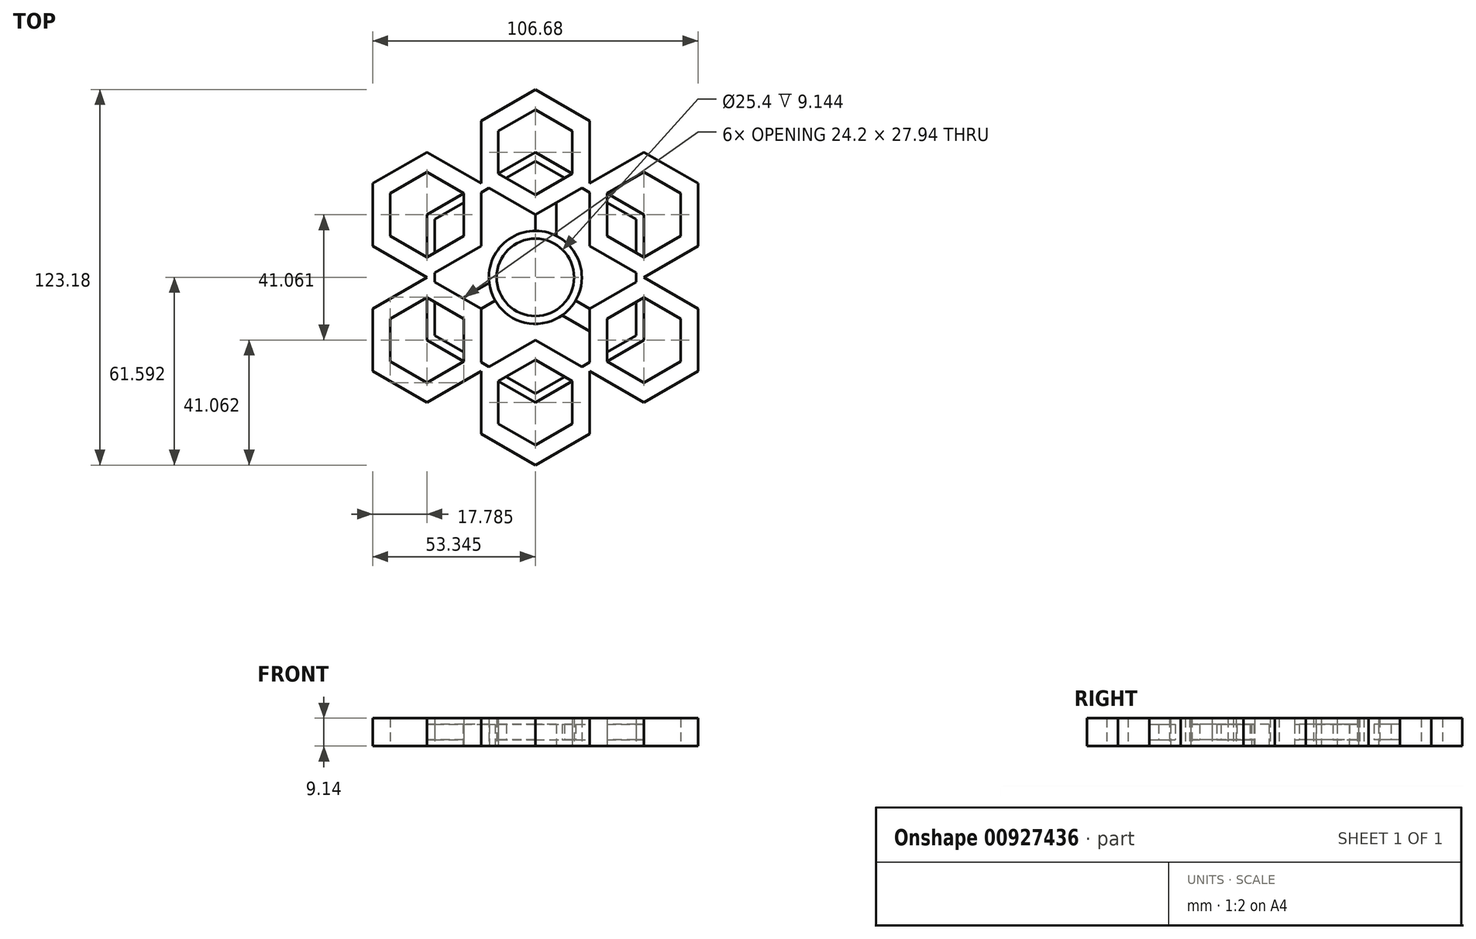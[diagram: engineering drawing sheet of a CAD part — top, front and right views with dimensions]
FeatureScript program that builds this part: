
annotation { "Feature Type Name" : "Feature", "Feature Type Description" : "" }
export const myFeature = defineFeature(function(context is Context, id is Id, definition is map)
    precondition{}
    {
        {
            var Q0;
            Q0=qCreatedBy(makeId("Top.planeOp"),FACE);
            var sketch = newSketch(context, id + "F0", { "sketchPlane" : qUnion([Q0])});
            skCircle(sketch, "E0", {"center": v(-0.28, 0.5) * mm, "radius": 12.7 * mm});
            skCircle(sketch, "E1.cCircle", {"center": v(-0.28, 0.5) * mm, "radius": 35.56 * mm, "construction": true});
            skLineSegment(sketch, "E1.0", {"start": v(35.28, 21.02) * mm, "end": v(35.28, -20.04) * mm});
            skLineSegment(sketch, "E1.1", {"start": v(35.28, -20.04) * mm, "end": v(-0.28, -40.57) * mm});
            skLineSegment(sketch, "E1.2", {"start": v(-0.28, -40.57) * mm, "end": v(-35.84, -20.04) * mm});
            skLineSegment(sketch, "E1.3", {"start": v(-35.84, -20.04) * mm, "end": v(-35.84, 21.02) * mm});
            skLineSegment(sketch, "E1.4", {"start": v(-35.84, 21.02) * mm, "end": v(-0.28, 41.55) * mm});
            skLineSegment(sketch, "E1.5", {"start": v(-0.28, 41.55) * mm, "end": v(35.28, 21.02) * mm});
            skPoint(sketch, "E1.0.midPoint", {"position": v(35.28, 0.5) * mm});
            skCircle(sketch, "E2.cCircle", {"center": v(35.28, 21.02) * mm, "radius": 20.53 * mm, "construction": true});
            skLineSegment(sketch, "E2.0", {"start": v(35.28, 0.5) * mm, "end": v(17.5, 10.76) * mm});
            skLineSegment(sketch, "E2.1", {"start": v(17.5, 10.76) * mm, "end": v(17.5, 31.29) * mm});
            skLineSegment(sketch, "E2.2", {"start": v(17.5, 31.29) * mm, "end": v(35.28, 41.55) * mm});
            skLineSegment(sketch, "E2.3", {"start": v(35.28, 41.55) * mm, "end": v(53.06, 31.29) * mm});
            skLineSegment(sketch, "E2.4", {"start": v(53.06, 31.29) * mm, "end": v(53.06, 10.76) * mm});
            skLineSegment(sketch, "E2.5", {"start": v(53.06, 10.76) * mm, "end": v(35.28, 0.5) * mm});
            skCircle(sketch, "E3.cCircle", {"center": v(-0.28, 41.55) * mm, "radius": 20.53 * mm, "construction": true});
            skLineSegment(sketch, "E3.0", {"start": v(17.5, 31.29) * mm, "end": v(-0.28, 21.02) * mm});
            skLineSegment(sketch, "E3.1", {"start": v(-0.28, 21.02) * mm, "end": v(-18.06, 31.29) * mm});
            skLineSegment(sketch, "E3.2", {"start": v(-18.06, 31.29) * mm, "end": v(-18.06, 51.82) * mm});
            skLineSegment(sketch, "E3.3", {"start": v(-18.06, 51.82) * mm, "end": v(-0.28, 62.08) * mm});
            skLineSegment(sketch, "E3.4", {"start": v(-0.28, 62.08) * mm, "end": v(17.5, 51.82) * mm});
            skLineSegment(sketch, "E3.5", {"start": v(17.5, 51.82) * mm, "end": v(17.5, 31.29) * mm});
            skCircle(sketch, "E4.cCircle", {"center": v(-35.84, 21.02) * mm, "radius": 20.53 * mm, "construction": true});
            skLineSegment(sketch, "E4.0", {"start": v(-18.06, 31.29) * mm, "end": v(-18.06, 10.76) * mm});
            skLineSegment(sketch, "E4.1", {"start": v(-18.06, 10.76) * mm, "end": v(-35.84, 0.5) * mm});
            skLineSegment(sketch, "E4.2", {"start": v(-35.84, 0.5) * mm, "end": v(-53.62, 10.76) * mm});
            skLineSegment(sketch, "E4.3", {"start": v(-53.62, 10.76) * mm, "end": v(-53.62, 31.29) * mm});
            skLineSegment(sketch, "E4.4", {"start": v(-53.62, 31.29) * mm, "end": v(-35.84, 41.55) * mm});
            skLineSegment(sketch, "E4.5", {"start": v(-35.84, 41.55) * mm, "end": v(-18.06, 31.29) * mm});
            skCircle(sketch, "E5.cCircle", {"center": v(-35.84, -20.04) * mm, "radius": 20.53 * mm, "construction": true});
            skLineSegment(sketch, "E5.0", {"start": v(-35.84, 0.5) * mm, "end": v(-18.06, -9.77) * mm});
            skLineSegment(sketch, "E5.1", {"start": v(-18.06, -9.77) * mm, "end": v(-18.06, -30.3) * mm});
            skLineSegment(sketch, "E5.2", {"start": v(-18.06, -30.3) * mm, "end": v(-35.84, -40.57) * mm});
            skLineSegment(sketch, "E5.3", {"start": v(-35.84, -40.57) * mm, "end": v(-53.62, -30.3) * mm});
            skLineSegment(sketch, "E5.4", {"start": v(-53.62, -30.3) * mm, "end": v(-53.62, -9.77) * mm});
            skLineSegment(sketch, "E5.5", {"start": v(-53.62, -9.77) * mm, "end": v(-35.84, 0.5) * mm});
            skCircle(sketch, "E6.cCircle", {"center": v(-0.28, -40.57) * mm, "radius": 20.53 * mm, "construction": true});
            skLineSegment(sketch, "E6.0", {"start": v(-18.06, -30.3) * mm, "end": v(-0.28, -20.04) * mm});
            skLineSegment(sketch, "E6.1", {"start": v(-0.28, -20.04) * mm, "end": v(17.5, -30.3) * mm});
            skLineSegment(sketch, "E6.2", {"start": v(17.5, -30.3) * mm, "end": v(17.5, -50.83) * mm});
            skLineSegment(sketch, "E6.3", {"start": v(17.5, -50.83) * mm, "end": v(-0.28, -61.1) * mm});
            skLineSegment(sketch, "E6.4", {"start": v(-0.28, -61.1) * mm, "end": v(-18.06, -50.83) * mm});
            skLineSegment(sketch, "E6.5", {"start": v(-18.06, -50.83) * mm, "end": v(-18.06, -30.3) * mm});
            skCircle(sketch, "E7.cCircle", {"center": v(35.28, -20.04) * mm, "radius": 20.53 * mm, "construction": true});
            skLineSegment(sketch, "E7.0", {"start": v(35.28, 0.5) * mm, "end": v(53.06, -9.77) * mm});
            skLineSegment(sketch, "E7.1", {"start": v(53.06, -9.77) * mm, "end": v(53.06, -30.3) * mm});
            skLineSegment(sketch, "E7.2", {"start": v(53.06, -30.3) * mm, "end": v(35.28, -40.57) * mm});
            skLineSegment(sketch, "E7.3", {"start": v(35.28, -40.57) * mm, "end": v(17.5, -30.3) * mm});
            skLineSegment(sketch, "E7.4", {"start": v(17.5, -30.3) * mm, "end": v(17.5, -9.77) * mm});
            skLineSegment(sketch, "E7.5", {"start": v(17.5, -9.77) * mm, "end": v(35.28, 0.5) * mm});
            skCircle(sketch, "E8.cCircle", {"center": v(-35.84, 21.02) * mm, "radius": 13.97 * mm, "construction": true});
            skLineSegment(sketch, "E8.0", {"start": v(-35.84, 7.05) * mm, "end": v(-47.93, 14.04) * mm});
            skLineSegment(sketch, "E8.1", {"start": v(-47.93, 14.04) * mm, "end": v(-47.93, 28) * mm});
            skLineSegment(sketch, "E8.2", {"start": v(-47.93, 28) * mm, "end": v(-35.84, 35) * mm});
            skLineSegment(sketch, "E8.3", {"start": v(-35.84, 35) * mm, "end": v(-23.74, 28) * mm});
            skLineSegment(sketch, "E8.4", {"start": v(-23.74, 28) * mm, "end": v(-23.74, 14.04) * mm});
            skLineSegment(sketch, "E8.5", {"start": v(-23.74, 14.04) * mm, "end": v(-35.84, 7.05) * mm});
            skCircle(sketch, "E9.cCircle", {"center": v(-0.28, 41.55) * mm, "radius": 13.97 * mm, "construction": true});
            skLineSegment(sketch, "E9.0", {"start": v(-0.28, 55.52) * mm, "end": v(11.82, 48.54) * mm});
            skLineSegment(sketch, "E9.1", {"start": v(11.82, 48.54) * mm, "end": v(11.82, 34.57) * mm});
            skLineSegment(sketch, "E9.2", {"start": v(11.82, 34.57) * mm, "end": v(-0.28, 27.58) * mm});
            skLineSegment(sketch, "E9.3", {"start": v(-0.28, 27.58) * mm, "end": v(-12.37, 34.57) * mm});
            skLineSegment(sketch, "E9.4", {"start": v(-12.37, 34.57) * mm, "end": v(-12.37, 48.54) * mm});
            skLineSegment(sketch, "E9.5", {"start": v(-12.37, 48.54) * mm, "end": v(-0.28, 55.52) * mm});
            skCircle(sketch, "E10.cCircle", {"center": v(35.28, 21.02) * mm, "radius": 13.97 * mm, "construction": true});
            skLineSegment(sketch, "E10.0", {"start": v(35.28, 7.05) * mm, "end": v(23.19, 14.04) * mm});
            skLineSegment(sketch, "E10.1", {"start": v(23.19, 14.04) * mm, "end": v(23.19, 28) * mm});
            skLineSegment(sketch, "E10.2", {"start": v(23.19, 28) * mm, "end": v(35.28, 35) * mm});
            skLineSegment(sketch, "E10.3", {"start": v(35.28, 35) * mm, "end": v(47.38, 28) * mm});
            skLineSegment(sketch, "E10.4", {"start": v(47.38, 28) * mm, "end": v(47.38, 14.04) * mm});
            skLineSegment(sketch, "E10.5", {"start": v(47.38, 14.04) * mm, "end": v(35.28, 7.05) * mm});
            skCircle(sketch, "E11.cCircle", {"center": v(35.28, -20.04) * mm, "radius": 13.97 * mm, "construction": true});
            skLineSegment(sketch, "E11.0", {"start": v(35.28, -34) * mm, "end": v(23.19, -27.02) * mm});
            skLineSegment(sketch, "E11.1", {"start": v(23.19, -27.02) * mm, "end": v(23.19, -13.05) * mm});
            skLineSegment(sketch, "E11.2", {"start": v(23.19, -13.05) * mm, "end": v(35.28, -6.07) * mm});
            skLineSegment(sketch, "E11.3", {"start": v(35.28, -6.07) * mm, "end": v(47.38, -13.05) * mm});
            skLineSegment(sketch, "E11.4", {"start": v(47.38, -13.05) * mm, "end": v(47.38, -27.02) * mm});
            skLineSegment(sketch, "E11.5", {"start": v(47.38, -27.02) * mm, "end": v(35.28, -34) * mm});
            skCircle(sketch, "E12.cCircle", {"center": v(-0.28, -40.57) * mm, "radius": 12.1 * mm, "construction": true});
            skLineSegment(sketch, "E12.0", {"start": v(-0.28, -54.54) * mm, "end": v(-12.37, -47.55) * mm});
            skLineSegment(sketch, "E12.1", {"start": v(-12.37, -47.55) * mm, "end": v(-12.37, -33.58) * mm});
            skLineSegment(sketch, "E12.2", {"start": v(-12.37, -33.58) * mm, "end": v(-0.28, -26.6) * mm});
            skLineSegment(sketch, "E12.3", {"start": v(-0.28, -26.6) * mm, "end": v(11.82, -33.58) * mm});
            skLineSegment(sketch, "E12.4", {"start": v(11.82, -33.58) * mm, "end": v(11.82, -47.55) * mm});
            skLineSegment(sketch, "E12.5", {"start": v(11.82, -47.55) * mm, "end": v(-0.28, -54.54) * mm});
            skPoint(sketch, "E12.0.midPoint", {"position": v(-6.32, -51.05) * mm});
            skCircle(sketch, "E13.cCircle", {"center": v(-35.84, -20.04) * mm, "radius": 13.97 * mm, "construction": true});
            skLineSegment(sketch, "E13.0", {"start": v(-35.84, -6.07) * mm, "end": v(-23.74, -13.05) * mm});
            skLineSegment(sketch, "E13.1", {"start": v(-23.74, -13.05) * mm, "end": v(-23.74, -27.02) * mm});
            skLineSegment(sketch, "E13.2", {"start": v(-23.74, -27.02) * mm, "end": v(-35.84, -34) * mm});
            skLineSegment(sketch, "E13.3", {"start": v(-35.84, -34) * mm, "end": v(-47.93, -27.02) * mm});
            skLineSegment(sketch, "E13.4", {"start": v(-47.93, -27.02) * mm, "end": v(-47.93, -13.05) * mm});
            skLineSegment(sketch, "E13.5", {"start": v(-47.93, -13.05) * mm, "end": v(-35.84, -6.07) * mm});
            skLineSegment(sketch, "E14", {"start": v(-18.06, -9.77) * mm, "end": v(-0.28, 0.5) * mm});
            skLineSegment(sketch, "E15", {"start": v(-0.28, 21.02) * mm, "end": v(-0.28, 0.5) * mm});
            skLineSegment(sketch, "E16", {"start": v(-0.28, 0.5) * mm, "end": v(17.5, -9.77) * mm});
            skLineSegment(sketch, "E17", {"start": v(-0.28, 0.5) * mm, "end": v(-0.28, -6.88) * mm});
            skLineSegment(sketch, "E18", {"start": v(-0.28, -6.88) * mm, "end": v(-0.28, 0.5) * mm});
            skLineSegment(sketch, "E19", {"start": v(-0.28, 0.5) * mm, "end": v(6.6, 4.46) * mm});
            skLineSegment(sketch, "E20", {"start": v(-0.28, 0.5) * mm, "end": v(-6.27, 3.95) * mm});
            skLineSegment(sketch, "E21", {"start": v(-6.27, 3.95) * mm, "end": v(-24.05, -6.31) * mm});
            skLineSegment(sketch, "E22", {"start": v(6.6, 4.46) * mm, "end": v(6.6, 24.99) * mm});
            skLineSegment(sketch, "E23", {"start": v(-0.28, -6.88) * mm, "end": v(17.5, -17.14) * mm});
            skCircle(sketch, "E24", {"center": v(-0.28, 0.5) * mm, "radius": 15.24 * mm});
            skCircle(sketch, "E25.cCircle", {"center": v(-0.28, 0.5) * mm, "radius": 38.1 * mm, "construction": true});
            skLineSegment(sketch, "E25.0", {"start": v(-0.28, 38.6) * mm, "end": v(32.72, 19.54) * mm});
            skLineSegment(sketch, "E25.1", {"start": v(32.72, 19.54) * mm, "end": v(32.72, -18.56) * mm});
            skLineSegment(sketch, "E25.2", {"start": v(32.72, -18.56) * mm, "end": v(-0.28, -37.6) * mm});
            skLineSegment(sketch, "E25.3", {"start": v(-0.28, -37.6) * mm, "end": v(-33.27, -18.56) * mm});
            skLineSegment(sketch, "E25.4", {"start": v(-33.27, -18.56) * mm, "end": v(-33.27, 19.54) * mm});
            skLineSegment(sketch, "E25.5", {"start": v(-33.27, 19.54) * mm, "end": v(-0.28, 38.6) * mm});
            skSolve(sketch);
        }
        {
            var Q0;
            {var subQ0=sQuery(id+"F0.wireOp",EDGE,"E4.2");Q0=makeQuery(id+"F0.imprint","IMPRINT",FACE,{"disambiguationData":[TD([[makeQuery(id+"F0.imprint","IMPRINT",EDGE,{"derivedFrom":subQ0}),-1.0]])]});}
            var Q1;
            {var subQ0=sQuery(id+"F0.wireOp",EDGE,"E4.1");var subQ5=sQuery(id+"F0.wireOp",EDGE,"E25.4");var subQ6=makeQuery(id+"F0.imprint","INTERSECT",VERTEX,{"derivedFrom":[subQ0,subQ5]});Q1=makeQuery(id+"F0.imprint","IMPRINT",FACE,{"disambiguationData":[TD([[makeQuery(id+"F0.imprint","IMPRINT",EDGE,{"disambiguationData":[TD([[subQ6,-1.0]])],"derivedFrom":subQ5}),1.0]])]});}
            var Q2;
            {var subQ3=sQuery(id+"F0.wireOp",EDGE,"E25.4");var subQ9=sQuery(id+"F0.wireOp",EDGE,"E25.5");var subQ11=makeQuery(id+"F0.imprint","INTERSECT",VERTEX,{"derivedFrom":[subQ3,subQ9]});Q2=makeQuery(id+"F0.imprint","IMPRINT",FACE,{"disambiguationData":[TD([[makeQuery(id+"F0.imprint","IMPRINT",EDGE,{"disambiguationData":[TD([[subQ11,1.0]])],"derivedFrom":subQ3}),1.0]])]});}
            var Q3;
            {var subQ0=sQuery(id+"F0.wireOp",EDGE,"E4.0");var subQ5=sQuery(id+"F0.wireOp",EDGE,"E25.5");var subQ6=makeQuery(id+"F0.imprint","INTERSECT",VERTEX,{"derivedFrom":[subQ0,subQ5]});Q3=makeQuery(id+"F0.imprint","IMPRINT",FACE,{"disambiguationData":[TD([[makeQuery(id+"F0.imprint","IMPRINT",EDGE,{"disambiguationData":[TD([[subQ6,1.0]])],"derivedFrom":subQ5}),1.0]])]});}
            var Q4;
            {var subQ7=sQuery(id+"F0.wireOp",EDGE,"E4.1");var subQ8=sQuery(id+"F0.wireOp",EDGE,"E4.0");var subQ9=makeQuery(id+"F0.imprint","INTERSECT",VERTEX,{"derivedFrom":[subQ8,subQ7]});Q4=makeQuery(id+"F0.imprint","IMPRINT",FACE,{"disambiguationData":[TD([[makeQuery(id+"F0.imprint","IMPRINT",EDGE,{"disambiguationData":[TD([[subQ9,1.0]])],"derivedFrom":subQ8}),-1.0]])]});}
            var Q5;
            {var subQ1=sQuery(id+"F0.wireOp",EDGE,"E4.1");var subQ3=sQuery(id+"F0.wireOp",EDGE,"E25.4");var subQ4=makeQuery(id+"F0.imprint","INTERSECT",VERTEX,{"derivedFrom":[subQ1,subQ3]});Q5=makeQuery(id+"F0.imprint","IMPRINT",FACE,{"disambiguationData":[TD([[makeQuery(id+"F0.imprint","IMPRINT",EDGE,{"disambiguationData":[TD([[subQ4,1.0]])],"derivedFrom":subQ3}),1.0]])]});}
            var Q6;
            {var subQ0=sQuery(id+"F0.wireOp",EDGE,"E5.0");var subQ5=sQuery(id+"F0.wireOp",EDGE,"E25.4");var subQ6=makeQuery(id+"F0.imprint","INTERSECT",VERTEX,{"derivedFrom":[subQ0,subQ5]});Q6=makeQuery(id+"F0.imprint","IMPRINT",FACE,{"disambiguationData":[TD([[makeQuery(id+"F0.imprint","IMPRINT",EDGE,{"disambiguationData":[TD([[subQ6,1.0]])],"derivedFrom":subQ5}),1.0]])]});}
            var Q7;
            {var subQ0=sQuery(id+"F0.wireOp",EDGE,"E5.2");Q7=makeQuery(id+"F0.imprint","IMPRINT",FACE,{"disambiguationData":[TD([[makeQuery(id+"F0.imprint","IMPRINT",EDGE,{"derivedFrom":subQ0}),-1.0]])]});}
            var Q8;
            {var subQ1=sQuery(id+"F0.wireOp",EDGE,"E5.0");var subQ10=makeQuery(id+"F0.imprint","INTERSECT",VERTEX,{"derivedFrom":[subQ1,sQuery(id+"F0.wireOp",EDGE,"E21")]});Q8=makeQuery(id+"F0.imprint","IMPRINT",FACE,{"disambiguationData":[TD([[makeQuery(id+"F0.imprint","IMPRINT",EDGE,{"disambiguationData":[TD([[subQ10,1.0]])],"derivedFrom":subQ1}),-1.0]])]});}
            var Q9;
            {var subQ3=sQuery(id+"F0.wireOp",EDGE,"E25.3");var subQ8=sQuery(id+"F0.wireOp",EDGE,"E25.4");var subQ10=makeQuery(id+"F0.imprint","INTERSECT",VERTEX,{"derivedFrom":[subQ3,subQ8]});Q9=makeQuery(id+"F0.imprint","IMPRINT",FACE,{"disambiguationData":[TD([[makeQuery(id+"F0.imprint","IMPRINT",EDGE,{"disambiguationData":[TD([[subQ10,1.0]])],"derivedFrom":subQ3}),1.0]])]});}
            var Q10;
            {var subQ0=sQuery(id+"F0.wireOp",EDGE,"E5.1");var subQ5=sQuery(id+"F0.wireOp",EDGE,"E25.3");var subQ6=makeQuery(id+"F0.imprint","INTERSECT",VERTEX,{"derivedFrom":[subQ0,subQ5]});Q10=makeQuery(id+"F0.imprint","IMPRINT",FACE,{"disambiguationData":[TD([[makeQuery(id+"F0.imprint","IMPRINT",EDGE,{"disambiguationData":[TD([[subQ6,-1.0]])],"derivedFrom":subQ5}),1.0]])]});}
            var Q11;
            {var subQ1=sQuery(id+"F0.wireOp",EDGE,"E5.0");var subQ3=sQuery(id+"F0.wireOp",EDGE,"E21");var subQ4=makeQuery(id+"F0.imprint","INTERSECT",VERTEX,{"derivedFrom":[subQ1,subQ3]});Q11=makeQuery(id+"F0.imprint","IMPRINT",FACE,{"disambiguationData":[TD([[makeQuery(id+"F0.imprint","IMPRINT",EDGE,{"disambiguationData":[TD([[subQ4,1.0]])],"derivedFrom":subQ3}),1.0]])]});}
            var Q12;
            {var subQ0=sQuery(id+"F0.wireOp",EDGE,"E21");var subQ1=sQuery(id+"F0.wireOp",EDGE,"E0");var subQ2=makeQuery(id+"F0.imprint","INTERSECT",VERTEX,{"derivedFrom":[subQ1,subQ0]});Q12=makeQuery(id+"F0.imprint","IMPRINT",FACE,{"disambiguationData":[TD([[makeQuery(id+"F0.imprint","IMPRINT",EDGE,{"disambiguationData":[TD([[subQ2,-1.0]])],"derivedFrom":subQ1}),-1.0]])]});}
            var Q13;
            {var subQ0=sQuery(id+"F0.wireOp",EDGE,"E15");var subQ1=sQuery(id+"F0.wireOp",EDGE,"E0");var subQ2=makeQuery(id+"F0.imprint","INTERSECT",VERTEX,{"derivedFrom":[subQ1,subQ0]});Q13=makeQuery(id+"F0.imprint","IMPRINT",FACE,{"disambiguationData":[TD([[makeQuery(id+"F0.imprint","IMPRINT",EDGE,{"disambiguationData":[TD([[subQ2,-1.0]])],"derivedFrom":subQ1}),-1.0]])]});}
            var Q14;
            {var subQ0=sQuery(id+"F0.wireOp",EDGE,"E15");var subQ1=sQuery(id+"F0.wireOp",EDGE,"E0");var subQ2=makeQuery(id+"F0.imprint","INTERSECT",VERTEX,{"derivedFrom":[subQ1,subQ0]});Q14=makeQuery(id+"F0.imprint","IMPRINT",FACE,{"disambiguationData":[TD([[makeQuery(id+"F0.imprint","IMPRINT",EDGE,{"disambiguationData":[TD([[subQ2,1.0]])],"derivedFrom":subQ1}),-1.0]])]});}
            var Q15;
            {var subQ1=sQuery(id+"F0.wireOp",EDGE,"E3.0");var subQ3=sQuery(id+"F0.wireOp",EDGE,"E22");var subQ4=makeQuery(id+"F0.imprint","INTERSECT",VERTEX,{"derivedFrom":[subQ1,subQ3]});Q15=makeQuery(id+"F0.imprint","IMPRINT",FACE,{"disambiguationData":[TD([[makeQuery(id+"F0.imprint","IMPRINT",EDGE,{"disambiguationData":[TD([[subQ4,1.0]])],"derivedFrom":subQ3}),1.0]])]});}
            var Q16;
            {var subQ0=sQuery(id+"F0.wireOp",EDGE,"E22");var subQ1=sQuery(id+"F0.wireOp",EDGE,"E0");var subQ2=makeQuery(id+"F0.imprint","INTERSECT",VERTEX,{"derivedFrom":[subQ1,subQ0]});Q16=makeQuery(id+"F0.imprint","IMPRINT",FACE,{"disambiguationData":[TD([[makeQuery(id+"F0.imprint","IMPRINT",EDGE,{"disambiguationData":[TD([[subQ2,1.0]])],"derivedFrom":subQ1}),-1.0]])]});}
            var Q17;
            {var subQ0=sQuery(id+"F0.wireOp",EDGE,"E23");var subQ1=sQuery(id+"F0.wireOp",EDGE,"E0");var subQ2=makeQuery(id+"F0.imprint","INTERSECT",VERTEX,{"derivedFrom":[subQ1,subQ0]});Q17=makeQuery(id+"F0.imprint","IMPRINT",FACE,{"disambiguationData":[TD([[makeQuery(id+"F0.imprint","IMPRINT",EDGE,{"disambiguationData":[TD([[subQ2,-1.0]])],"derivedFrom":subQ1}),-1.0]])]});}
            var Q18;
            {var subQ0=sQuery(id+"F0.wireOp",EDGE,"E14");var subQ1=sQuery(id+"F0.wireOp",EDGE,"E0");var subQ2=makeQuery(id+"F0.imprint","INTERSECT",VERTEX,{"derivedFrom":[subQ1,subQ0]});Q18=makeQuery(id+"F0.imprint","IMPRINT",FACE,{"disambiguationData":[TD([[makeQuery(id+"F0.imprint","IMPRINT",EDGE,{"disambiguationData":[TD([[subQ2,-1.0]])],"derivedFrom":subQ1}),-1.0]])]});}
            var Q19;
            {var subQ1=sQuery(id+"F0.wireOp",EDGE,"E7.4");var subQ3=sQuery(id+"F0.wireOp",EDGE,"E23");var subQ4=makeQuery(id+"F0.imprint","INTERSECT",VERTEX,{"derivedFrom":[subQ1,subQ3]});Q19=makeQuery(id+"F0.imprint","IMPRINT",FACE,{"disambiguationData":[TD([[makeQuery(id+"F0.imprint","IMPRINT",EDGE,{"disambiguationData":[TD([[subQ4,1.0]])],"derivedFrom":subQ3}),1.0]])]});}
            var Q20;
            {var subQ1=sQuery(id+"F0.wireOp",EDGE,"E5.1");var subQ3=sQuery(id+"F0.wireOp",EDGE,"E25.3");var subQ4=makeQuery(id+"F0.imprint","INTERSECT",VERTEX,{"derivedFrom":[subQ1,subQ3]});Q20=makeQuery(id+"F0.imprint","IMPRINT",FACE,{"disambiguationData":[TD([[makeQuery(id+"F0.imprint","IMPRINT",EDGE,{"disambiguationData":[TD([[subQ4,1.0]])],"derivedFrom":subQ3}),1.0]])]});}
            var Q21;
            {var subQ0=sQuery(id+"F0.wireOp",EDGE,"E6.0");var subQ5=sQuery(id+"F0.wireOp",EDGE,"E25.3");var subQ7=makeQuery(id+"F0.imprint","INTERSECT",VERTEX,{"derivedFrom":[subQ0,subQ5]});Q21=makeQuery(id+"F0.imprint","IMPRINT",FACE,{"disambiguationData":[TD([[makeQuery(id+"F0.imprint","IMPRINT",EDGE,{"disambiguationData":[TD([[subQ7,1.0]])],"derivedFrom":subQ5}),1.0]])]});}
            var Q22;
            {var subQ6=sQuery(id+"F0.wireOp",EDGE,"E6.0");var subQ9=sQuery(id+"F0.wireOp",EDGE,"E6.1");var subQ10=makeQuery(id+"F0.imprint","INTERSECT",VERTEX,{"derivedFrom":[subQ6,subQ9]});Q22=makeQuery(id+"F0.imprint","IMPRINT",FACE,{"disambiguationData":[TD([[makeQuery(id+"F0.imprint","IMPRINT",EDGE,{"disambiguationData":[TD([[subQ10,1.0]])],"derivedFrom":subQ6}),-1.0]])]});}
            var Q23;
            {var subQ0=sQuery(id+"F0.wireOp",EDGE,"E6.2");Q23=makeQuery(id+"F0.imprint","IMPRINT",FACE,{"disambiguationData":[TD([[makeQuery(id+"F0.imprint","IMPRINT",EDGE,{"derivedFrom":subQ0}),-1.0]])]});}
            var Q24;
            {var subQ3=sQuery(id+"F0.wireOp",EDGE,"E25.3");var subQ5=sQuery(id+"F0.wireOp",EDGE,"E25.2");var subQ6=makeQuery(id+"F0.imprint","INTERSECT",VERTEX,{"derivedFrom":[subQ5,subQ3]});Q24=makeQuery(id+"F0.imprint","IMPRINT",FACE,{"disambiguationData":[TD([[makeQuery(id+"F0.imprint","IMPRINT",EDGE,{"disambiguationData":[TD([[subQ6,1.0]])],"derivedFrom":subQ5}),1.0]])]});}
            var Q25;
            {var subQ0=sQuery(id+"F0.wireOp",EDGE,"E6.1");var subQ5=sQuery(id+"F0.wireOp",EDGE,"E25.2");var subQ6=makeQuery(id+"F0.imprint","INTERSECT",VERTEX,{"derivedFrom":[subQ0,subQ5]});Q25=makeQuery(id+"F0.imprint","IMPRINT",FACE,{"disambiguationData":[TD([[makeQuery(id+"F0.imprint","IMPRINT",EDGE,{"disambiguationData":[TD([[subQ6,-1.0]])],"derivedFrom":subQ5}),1.0]])]});}
            var Q26;
            {var subQ1=sQuery(id+"F0.wireOp",EDGE,"E7.4");var subQ9=makeQuery(id+"F0.imprint","INTERSECT",VERTEX,{"derivedFrom":[subQ1,sQuery(id+"F0.wireOp",EDGE,"E23")]});Q26=makeQuery(id+"F0.imprint","IMPRINT",FACE,{"disambiguationData":[TD([[makeQuery(id+"F0.imprint","IMPRINT",EDGE,{"disambiguationData":[TD([[subQ9,1.0]])],"derivedFrom":subQ1}),-1.0]])]});}
            var Q27;
            {var subQ0=sQuery(id+"F0.wireOp",EDGE,"E7.4");var subQ5=sQuery(id+"F0.wireOp",EDGE,"E25.2");var subQ6=makeQuery(id+"F0.imprint","INTERSECT",VERTEX,{"derivedFrom":[subQ0,subQ5]});Q27=makeQuery(id+"F0.imprint","IMPRINT",FACE,{"disambiguationData":[TD([[makeQuery(id+"F0.imprint","IMPRINT",EDGE,{"disambiguationData":[TD([[subQ6,1.0]])],"derivedFrom":subQ5}),1.0]])]});}
            var Q28;
            {var subQ1=sQuery(id+"F0.wireOp",EDGE,"E6.1");var subQ3=sQuery(id+"F0.wireOp",EDGE,"E25.2");var subQ4=makeQuery(id+"F0.imprint","INTERSECT",VERTEX,{"derivedFrom":[subQ1,subQ3]});Q28=makeQuery(id+"F0.imprint","IMPRINT",FACE,{"disambiguationData":[TD([[makeQuery(id+"F0.imprint","IMPRINT",EDGE,{"disambiguationData":[TD([[subQ4,1.0]])],"derivedFrom":subQ3}),1.0]])]});}
            var Q29;
            {var subQ0=sQuery(id+"F0.wireOp",EDGE,"E7.5");var subQ5=sQuery(id+"F0.wireOp",EDGE,"E25.1");var subQ6=makeQuery(id+"F0.imprint","INTERSECT",VERTEX,{"derivedFrom":[subQ0,subQ5]});Q29=makeQuery(id+"F0.imprint","IMPRINT",FACE,{"disambiguationData":[TD([[makeQuery(id+"F0.imprint","IMPRINT",EDGE,{"disambiguationData":[TD([[subQ6,-1.0]])],"derivedFrom":subQ5}),1.0]])]});}
            var Q30;
            {var subQ0=sQuery(id+"F0.wireOp",EDGE,"E7.0");Q30=makeQuery(id+"F0.imprint","IMPRINT",FACE,{"disambiguationData":[TD([[makeQuery(id+"F0.imprint","IMPRINT",EDGE,{"derivedFrom":subQ0}),-1.0]])]});}
            var Q31;
            {var subQ3=sQuery(id+"F0.wireOp",EDGE,"E25.2");var subQ9=sQuery(id+"F0.wireOp",EDGE,"E25.1");var subQ11=makeQuery(id+"F0.imprint","INTERSECT",VERTEX,{"derivedFrom":[subQ9,subQ3]});Q31=makeQuery(id+"F0.imprint","IMPRINT",FACE,{"disambiguationData":[TD([[makeQuery(id+"F0.imprint","IMPRINT",EDGE,{"disambiguationData":[TD([[subQ11,1.0]])],"derivedFrom":subQ9}),1.0]])]});}
            var Q32;
            {var subQ1=sQuery(id+"F0.wireOp",EDGE,"E2.0");var subQ3=sQuery(id+"F0.wireOp",EDGE,"E25.1");var subQ4=makeQuery(id+"F0.imprint","INTERSECT",VERTEX,{"derivedFrom":[subQ1,subQ3]});Q32=makeQuery(id+"F0.imprint","IMPRINT",FACE,{"disambiguationData":[TD([[makeQuery(id+"F0.imprint","IMPRINT",EDGE,{"disambiguationData":[TD([[subQ4,-1.0]])],"derivedFrom":subQ3}),1.0]])]});}
            var Q33;
            {var subQ0=sQuery(id+"F0.wireOp",EDGE,"E2.0");var subQ5=sQuery(id+"F0.wireOp",EDGE,"E25.1");var subQ7=makeQuery(id+"F0.imprint","INTERSECT",VERTEX,{"derivedFrom":[subQ0,subQ5]});Q33=makeQuery(id+"F0.imprint","IMPRINT",FACE,{"disambiguationData":[TD([[makeQuery(id+"F0.imprint","IMPRINT",EDGE,{"disambiguationData":[TD([[subQ7,1.0]])],"derivedFrom":subQ5}),1.0]])]});}
            var Q34;
            {var subQ7=sQuery(id+"F0.wireOp",EDGE,"E2.1");var subQ8=sQuery(id+"F0.wireOp",EDGE,"E2.0");var subQ9=makeQuery(id+"F0.imprint","INTERSECT",VERTEX,{"derivedFrom":[subQ8,subQ7]});Q34=makeQuery(id+"F0.imprint","IMPRINT",FACE,{"disambiguationData":[TD([[makeQuery(id+"F0.imprint","IMPRINT",EDGE,{"disambiguationData":[TD([[subQ9,1.0]])],"derivedFrom":subQ8}),-1.0]])]});}
            var Q35;
            {var subQ1=sQuery(id+"F0.wireOp",EDGE,"E2.2");Q35=makeQuery(id+"F0.imprint","IMPRINT",FACE,{"disambiguationData":[TD([[makeQuery(id+"F0.imprint","IMPRINT",EDGE,{"derivedFrom":subQ1}),-1.0]])]});}
            var Q36;
            {var subQ3=sQuery(id+"F0.wireOp",EDGE,"E25.0");var subQ8=sQuery(id+"F0.wireOp",EDGE,"E25.1");var subQ11=makeQuery(id+"F0.imprint","INTERSECT",VERTEX,{"derivedFrom":[subQ3,subQ8]});Q36=makeQuery(id+"F0.imprint","IMPRINT",FACE,{"disambiguationData":[TD([[makeQuery(id+"F0.imprint","IMPRINT",EDGE,{"disambiguationData":[TD([[subQ11,1.0]])],"derivedFrom":subQ3}),1.0]])]});}
            var Q37;
            {var subQ0=sQuery(id+"F0.wireOp",EDGE,"E2.1");var subQ5=sQuery(id+"F0.wireOp",EDGE,"E25.0");var subQ6=makeQuery(id+"F0.imprint","INTERSECT",VERTEX,{"derivedFrom":[subQ0,subQ5]});Q37=makeQuery(id+"F0.imprint","IMPRINT",FACE,{"disambiguationData":[TD([[makeQuery(id+"F0.imprint","IMPRINT",EDGE,{"disambiguationData":[TD([[subQ6,-1.0]])],"derivedFrom":subQ5}),1.0]])]});}
            var Q38;
            {var subQ1=sQuery(id+"F0.wireOp",EDGE,"E2.1");var subQ3=sQuery(id+"F0.wireOp",EDGE,"E25.0");var subQ4=makeQuery(id+"F0.imprint","INTERSECT",VERTEX,{"derivedFrom":[subQ1,subQ3]});Q38=makeQuery(id+"F0.imprint","IMPRINT",FACE,{"disambiguationData":[TD([[makeQuery(id+"F0.imprint","IMPRINT",EDGE,{"disambiguationData":[TD([[subQ4,1.0]])],"derivedFrom":subQ3}),1.0]])]});}
            var Q39;
            {var subQ0=sQuery(id+"F0.wireOp",EDGE,"E3.0");var subQ5=sQuery(id+"F0.wireOp",EDGE,"E25.0");var subQ6=makeQuery(id+"F0.imprint","INTERSECT",VERTEX,{"derivedFrom":[subQ0,subQ5]});Q39=makeQuery(id+"F0.imprint","IMPRINT",FACE,{"disambiguationData":[TD([[makeQuery(id+"F0.imprint","IMPRINT",EDGE,{"disambiguationData":[TD([[subQ6,1.0]])],"derivedFrom":subQ5}),1.0]])]});}
            var Q40;
            {var subQ6=sQuery(id+"F0.wireOp",EDGE,"E3.0");var subQ11=makeQuery(id+"F0.imprint","INTERSECT",VERTEX,{"derivedFrom":[subQ6,sQuery(id+"F0.wireOp",EDGE,"E22")]});Q40=makeQuery(id+"F0.imprint","IMPRINT",FACE,{"disambiguationData":[TD([[makeQuery(id+"F0.imprint","IMPRINT",EDGE,{"disambiguationData":[TD([[subQ11,1.0]])],"derivedFrom":subQ6}),-1.0]])]});}
            var Q41;
            {var subQ0=sQuery(id+"F0.wireOp",EDGE,"E3.2");Q41=makeQuery(id+"F0.imprint","IMPRINT",FACE,{"disambiguationData":[TD([[makeQuery(id+"F0.imprint","IMPRINT",EDGE,{"derivedFrom":subQ0}),-1.0]])]});}
            var Q42;
            {var subQ3=sQuery(id+"F0.wireOp",EDGE,"E25.5");var subQ8=sQuery(id+"F0.wireOp",EDGE,"E25.0");var subQ11=makeQuery(id+"F0.imprint","INTERSECT",VERTEX,{"derivedFrom":[subQ8,subQ3]});Q42=makeQuery(id+"F0.imprint","IMPRINT",FACE,{"disambiguationData":[TD([[makeQuery(id+"F0.imprint","IMPRINT",EDGE,{"disambiguationData":[TD([[subQ11,-1.0]])],"derivedFrom":subQ8}),1.0]])]});}
            var Q43;
            {var subQ0=sQuery(id+"F0.wireOp",EDGE,"E3.1");var subQ5=sQuery(id+"F0.wireOp",EDGE,"E25.5");var subQ7=makeQuery(id+"F0.imprint","INTERSECT",VERTEX,{"derivedFrom":[subQ0,subQ5]});Q43=makeQuery(id+"F0.imprint","IMPRINT",FACE,{"disambiguationData":[TD([[makeQuery(id+"F0.imprint","IMPRINT",EDGE,{"disambiguationData":[TD([[subQ7,-1.0]])],"derivedFrom":subQ5}),1.0]])]});}
            var Q44;
            {var subQ1=sQuery(id+"F0.wireOp",EDGE,"E3.1");var subQ3=sQuery(id+"F0.wireOp",EDGE,"E25.5");var subQ4=makeQuery(id+"F0.imprint","INTERSECT",VERTEX,{"derivedFrom":[subQ1,subQ3]});Q44=makeQuery(id+"F0.imprint","IMPRINT",FACE,{"disambiguationData":[TD([[makeQuery(id+"F0.imprint","IMPRINT",EDGE,{"disambiguationData":[TD([[subQ4,1.0]])],"derivedFrom":subQ3}),1.0]])]});}
            extrude(context, id + "F1", {"entities" : qUnion([Q0, Q1, Q2, Q3, Q4, Q5, Q6, Q7, Q8, Q9, Q10, Q11, Q12, Q13, Q14, Q15, Q16, Q17, Q18, Q19, Q20, Q21, Q22, Q23, Q24, Q25, Q26, Q27, Q28, Q29, Q30, Q31, Q32, Q33, Q34, Q35, Q36, Q37, Q38, Q39, Q40, Q41, Q42, Q43, Q44]), "depth" : 4.57 * mm, "offsetDistance" : 25.4 * mm, "hasSecondDirection" : true, "secondDirectionOppositeDirection" : true, "secondDirectionDepth" : 4.57 * mm});
        }
        {
            var Q0;
            Q0=makeQuery(id+"F1.opExtrude","CAP_FACE",FACE,{"disambiguationData":[OSD([sQuery(id+"F0.wireOp",EDGE,"E0"),sQuery(id+"F0.wireOp",EDGE,"E1.0"),sQuery(id+"F0.wireOp",EDGE,"E1.1"),sQuery(id+"F0.wireOp",EDGE,"E1.2"),sQuery(id+"F0.wireOp",EDGE,"E1.3"),sQuery(id+"F0.wireOp",EDGE,"E1.4"),sQuery(id+"F0.wireOp",EDGE,"E1.5"),sQuery(id+"F0.wireOp",EDGE,"E2.0"),sQuery(id+"F0.wireOp",EDGE,"E2.1"),sQuery(id+"F0.wireOp",EDGE,"E2.2"),sQuery(id+"F0.wireOp",EDGE,"E2.3"),sQuery(id+"F0.wireOp",EDGE,"E2.4"),sQuery(id+"F0.wireOp",EDGE,"E2.5"),sQuery(id+"F0.wireOp",EDGE,"E3.0"),sQuery(id+"F0.wireOp",EDGE,"E3.1"),sQuery(id+"F0.wireOp",EDGE,"E3.2"),sQuery(id+"F0.wireOp",EDGE,"E3.3"),sQuery(id+"F0.wireOp",EDGE,"E3.4"),sQuery(id+"F0.wireOp",EDGE,"E3.5"),sQuery(id+"F0.wireOp",EDGE,"E4.0"),sQuery(id+"F0.wireOp",EDGE,"E4.1"),sQuery(id+"F0.wireOp",EDGE,"E4.2"),sQuery(id+"F0.wireOp",EDGE,"E4.3"),sQuery(id+"F0.wireOp",EDGE,"E4.4"),sQuery(id+"F0.wireOp",EDGE,"E4.5"),sQuery(id+"F0.wireOp",EDGE,"E5.0"),sQuery(id+"F0.wireOp",EDGE,"E5.1"),sQuery(id+"F0.wireOp",EDGE,"E5.2"),sQuery(id+"F0.wireOp",EDGE,"E5.3"),sQuery(id+"F0.wireOp",EDGE,"E5.4"),sQuery(id+"F0.wireOp",EDGE,"E5.5"),sQuery(id+"F0.wireOp",EDGE,"E6.0"),sQuery(id+"F0.wireOp",EDGE,"E6.1"),sQuery(id+"F0.wireOp",EDGE,"E6.2"),sQuery(id+"F0.wireOp",EDGE,"E6.3"),sQuery(id+"F0.wireOp",EDGE,"E6.4"),sQuery(id+"F0.wireOp",EDGE,"E6.5"),sQuery(id+"F0.wireOp",EDGE,"E7.0"),sQuery(id+"F0.wireOp",EDGE,"E7.1"),sQuery(id+"F0.wireOp",EDGE,"E7.2"),sQuery(id+"F0.wireOp",EDGE,"E7.3"),sQuery(id+"F0.wireOp",EDGE,"E7.4"),sQuery(id+"F0.wireOp",EDGE,"E7.5"),sQuery(id+"F0.wireOp",EDGE,"E8.0"),sQuery(id+"F0.wireOp",EDGE,"E8.1"),sQuery(id+"F0.wireOp",EDGE,"E8.2"),sQuery(id+"F0.wireOp",EDGE,"E8.3"),sQuery(id+"F0.wireOp",EDGE,"E8.4"),sQuery(id+"F0.wireOp",EDGE,"E8.5"),sQuery(id+"F0.wireOp",EDGE,"E9.0"),sQuery(id+"F0.wireOp",EDGE,"E9.1"),sQuery(id+"F0.wireOp",EDGE,"E9.2"),sQuery(id+"F0.wireOp",EDGE,"E9.3"),sQuery(id+"F0.wireOp",EDGE,"E9.4"),sQuery(id+"F0.wireOp",EDGE,"E9.5"),sQuery(id+"F0.wireOp",EDGE,"E10.0"),sQuery(id+"F0.wireOp",EDGE,"E10.1"),sQuery(id+"F0.wireOp",EDGE,"E10.2"),sQuery(id+"F0.wireOp",EDGE,"E10.3"),sQuery(id+"F0.wireOp",EDGE,"E10.4"),sQuery(id+"F0.wireOp",EDGE,"E10.5"),sQuery(id+"F0.wireOp",EDGE,"E11.0"),sQuery(id+"F0.wireOp",EDGE,"E11.1"),sQuery(id+"F0.wireOp",EDGE,"E11.2"),sQuery(id+"F0.wireOp",EDGE,"E11.3"),sQuery(id+"F0.wireOp",EDGE,"E11.4"),sQuery(id+"F0.wireOp",EDGE,"E11.5"),sQuery(id+"F0.wireOp",EDGE,"E12.0"),sQuery(id+"F0.wireOp",EDGE,"E12.1"),sQuery(id+"F0.wireOp",EDGE,"E12.2"),sQuery(id+"F0.wireOp",EDGE,"E12.3"),sQuery(id+"F0.wireOp",EDGE,"E12.4"),sQuery(id+"F0.wireOp",EDGE,"E12.5"),sQuery(id+"F0.wireOp",EDGE,"E13.0"),sQuery(id+"F0.wireOp",EDGE,"E13.1"),sQuery(id+"F0.wireOp",EDGE,"E13.2"),sQuery(id+"F0.wireOp",EDGE,"E13.3"),sQuery(id+"F0.wireOp",EDGE,"E13.4"),sQuery(id+"F0.wireOp",EDGE,"E13.5"),sQuery(id+"F0.wireOp",EDGE,"E14"),sQuery(id+"F0.wireOp",EDGE,"E15"),sQuery(id+"F0.wireOp",EDGE,"E16"),sQuery(id+"F0.wireOp",EDGE,"E21"),sQuery(id+"F0.wireOp",EDGE,"E22"),sQuery(id+"F0.wireOp",EDGE,"E23"),sQuery(id+"F0.wireOp",EDGE,"E24"),sQuery(id+"F0.wireOp",EDGE,"E25.0"),sQuery(id+"F0.wireOp",EDGE,"E25.1"),sQuery(id+"F0.wireOp",EDGE,"E25.2"),sQuery(id+"F0.wireOp",EDGE,"E25.3"),sQuery(id+"F0.wireOp",EDGE,"E25.4"),sQuery(id+"F0.wireOp",EDGE,"E25.5")])],"isStart":true});
            var sketch = newSketch(context, id + "F2", { "sketchPlane" : qUnion([Q0])});
            skLineSegment(sketch, "E26.0", {"start": v(-35.84, 40.57) * mm, "end": v(-53.62, 30.3) * mm});
            skLineSegment(sketch, "E26.1", {"start": v(-0.28, 37.6) * mm, "end": v(-33.27, 18.56) * mm});
            skLineSegment(sketch, "E26.2", {"start": v(-35.84, 34) * mm, "end": v(-47.93, 27.02) * mm});
            skLineSegment(sketch, "E26.3", {"start": v(47.38, -14.04) * mm, "end": v(35.28, -7.05) * mm});
            skLineSegment(sketch, "E26.4", {"start": v(-47.93, -14.04) * mm, "end": v(-47.93, -28) * mm});
            skLineSegment(sketch, "E26.5", {"start": v(-18.06, 9.77) * mm, "end": v(-18.06, 30.3) * mm});
            skCircle(sketch, "E26.6", {"center": v(-35.84, 20.04) * mm, "radius": 13.97 * mm});
            skLineSegment(sketch, "E26.7", {"start": v(32.72, -19.54) * mm, "end": v(32.72, 18.56) * mm});
            skLineSegment(sketch, "E26.8", {"start": v(-23.74, 13.05) * mm, "end": v(-23.74, 27.02) * mm});
            skLineSegment(sketch, "E26.9", {"start": v(35.28, -35) * mm, "end": v(47.38, -28) * mm});
            skLineSegment(sketch, "E26.10", {"start": v(17.5, 9.77) * mm, "end": v(35.28, -0.5) * mm});
            skLineSegment(sketch, "E26.11", {"start": v(-35.84, -41.55) * mm, "end": v(-18.06, -31.29) * mm});
            skCircle(sketch, "E26.12", {"center": v(35.28, 20.04) * mm, "radius": 13.97 * mm});
            skLineSegment(sketch, "E26.13", {"start": v(-0.28, 6.88) * mm, "end": v(17.5, 17.14) * mm});
            skLineSegment(sketch, "E26.14", {"start": v(11.82, 47.55) * mm, "end": v(-0.28, 54.54) * mm});
            skLineSegment(sketch, "E26.15", {"start": v(23.19, -14.04) * mm, "end": v(23.19, -28) * mm});
            skLineSegment(sketch, "E26.16", {"start": v(35.28, 40.57) * mm, "end": v(17.5, 30.3) * mm});
            skCircle(sketch, "E26.17", {"center": v(-0.28, -41.55) * mm, "radius": 13.97 * mm});
            skLineSegment(sketch, "E26.18", {"start": v(-35.84, -35) * mm, "end": v(-23.74, -28) * mm});
            skLineSegment(sketch, "E26.19", {"start": v(-12.37, -34.57) * mm, "end": v(-12.37, -48.54) * mm});
            skLineSegment(sketch, "E26.20", {"start": v(35.28, -0.5) * mm, "end": v(53.06, 9.77) * mm});
            skLineSegment(sketch, "E26.21", {"start": v(-53.62, 9.77) * mm, "end": v(-35.84, -0.5) * mm});
            skLineSegment(sketch, "E26.22", {"start": v(-35.84, -0.5) * mm, "end": v(-53.62, -10.76) * mm});
            skArc(sketch, "E26.23", {"start": v(-29.9, 23.46) * mm, "mid": v(-19.33, 32.5) * mm, "end": v(-6.2, 37.14) * mm});
            skLineSegment(sketch, "E26.24", {"start": v(-33.27, -19.54) * mm, "end": v(-0.28, -38.6) * mm});
            skArc(sketch, "E26.25", {"start": v(-18.06, 30.3) * mm, "mid": v(-0.28, 61.1) * mm, "end": v(17.5, 30.3) * mm});
            skLineSegment(sketch, "E26.26", {"start": v(-47.93, 13.05) * mm, "end": v(-35.84, 6.07) * mm});
            skLineSegment(sketch, "E26.27", {"start": v(23.19, 27.02) * mm, "end": v(23.19, 13.05) * mm});
            skLineSegment(sketch, "E26.28", {"start": v(-12.37, 33.58) * mm, "end": v(-0.28, 26.6) * mm});
            skLineSegment(sketch, "E26.29", {"start": v(11.82, -34.57) * mm, "end": v(-0.28, -27.58) * mm});
            skLineSegment(sketch, "E26.30", {"start": v(-0.28, 61.1) * mm, "end": v(-18.06, 50.83) * mm});
            skLineSegment(sketch, "E26.31", {"start": v(-18.06, -31.29) * mm, "end": v(-18.06, -10.76) * mm});
            skArc(sketch, "E26.32", {"start": v(-33.27, -0.65) * mm, "mid": v(-18.06, -10.76) * mm, "end": v(-16.91, -28.99) * mm});
            skLineSegment(sketch, "E26.33", {"start": v(-0.28, -55.52) * mm, "end": v(11.82, -48.54) * mm});
            skLineSegment(sketch, "E26.34", {"start": v(17.5, 30.3) * mm, "end": v(17.5, 50.83) * mm});
            skLineSegment(sketch, "E26.35", {"start": v(-0.28, -62.08) * mm, "end": v(17.5, -51.82) * mm});
            skArc(sketch, "E26.36", {"start": v(35.28, -0.5) * mm, "mid": v(53.06, -31.29) * mm, "end": v(17.5, -31.29) * mm});
            skLineSegment(sketch, "E26.37", {"start": v(-0.28, -0.5) * mm, "end": v(17.5, 9.77) * mm});
            skLineSegment(sketch, "E26.38", {"start": v(47.38, 13.05) * mm, "end": v(47.38, 27.02) * mm});
            skLineSegment(sketch, "E26.39", {"start": v(-18.06, -51.82) * mm, "end": v(-0.28, -62.08) * mm});
            skLineSegment(sketch, "E26.40", {"start": v(-0.28, -21.02) * mm, "end": v(-18.06, -31.29) * mm});
            skLineSegment(sketch, "E26.41", {"start": v(-18.06, -31.29) * mm, "end": v(-18.06, -51.82) * mm});
            skLineSegment(sketch, "E26.42", {"start": v(-53.62, 30.3) * mm, "end": v(-53.62, 9.77) * mm});
            skLineSegment(sketch, "E26.43", {"start": v(-33.27, 18.56) * mm, "end": v(-33.27, -19.54) * mm});
            skLineSegment(sketch, "E26.44", {"start": v(-47.93, 27.02) * mm, "end": v(-47.93, 13.05) * mm});
            skLineSegment(sketch, "E26.45", {"start": v(35.28, 34) * mm, "end": v(23.19, 27.02) * mm});
            skLineSegment(sketch, "E26.46", {"start": v(-47.93, -28) * mm, "end": v(-35.84, -35) * mm});
            skLineSegment(sketch, "E26.47", {"start": v(-18.06, 30.3) * mm, "end": v(-35.84, 40.57) * mm});
            skLineSegment(sketch, "E26.48", {"start": v(35.28, -21.02) * mm, "end": v(35.28, 20.04) * mm});
            skCircle(sketch, "E26.49", {"center": v(-0.28, -0.5) * mm, "radius": 15.24 * mm});
            skLineSegment(sketch, "E26.50", {"start": v(32.72, 18.56) * mm, "end": v(-0.28, 37.6) * mm});
            skLineSegment(sketch, "E26.51", {"start": v(35.28, 20.04) * mm, "end": v(-0.28, 40.57) * mm});
            skLineSegment(sketch, "E26.52", {"start": v(-23.74, 27.02) * mm, "end": v(-35.84, 34) * mm});
            skLineSegment(sketch, "E26.53", {"start": v(47.38, -28) * mm, "end": v(47.38, -14.04) * mm});
            skLineSegment(sketch, "E26.54", {"start": v(-35.84, -7.05) * mm, "end": v(-47.93, -14.04) * mm});
            skLineSegment(sketch, "E26.55", {"start": v(-35.84, -0.5) * mm, "end": v(-18.06, 9.77) * mm});
            skLineSegment(sketch, "E26.56", {"start": v(-0.28, 40.57) * mm, "end": v(-35.84, 20.04) * mm});
            skArc(sketch, "E26.57", {"start": v(-10.75, 34.52) * mm, "mid": v(-0.28, 52.67) * mm, "end": v(10.2, 34.52) * mm});
            skLineSegment(sketch, "E26.58", {"start": v(-0.28, -38.6) * mm, "end": v(32.72, -19.54) * mm});
            skLineSegment(sketch, "E26.59", {"start": v(-35.84, 6.07) * mm, "end": v(-23.74, 13.05) * mm});
            skLineSegment(sketch, "E26.60", {"start": v(-35.84, 20.04) * mm, "end": v(-35.84, -21.02) * mm});
            skLineSegment(sketch, "E26.61", {"start": v(23.19, -28) * mm, "end": v(35.28, -35) * mm});
            skLineSegment(sketch, "E26.62", {"start": v(17.5, 30.3) * mm, "end": v(17.5, 9.77) * mm});
            skLineSegment(sketch, "E26.63", {"start": v(-53.62, -31.29) * mm, "end": v(-35.84, -41.55) * mm});
            skLineSegment(sketch, "E26.64", {"start": v(-35.84, -21.02) * mm, "end": v(-0.28, -41.55) * mm});
            skCircle(sketch, "E26.65", {"center": v(35.28, -21.02) * mm, "radius": 13.97 * mm});
            skLineSegment(sketch, "E26.66", {"start": v(6.6, -4.46) * mm, "end": v(6.6, -24.99) * mm});
            skLineSegment(sketch, "E26.67", {"start": v(11.82, 33.58) * mm, "end": v(11.82, 47.55) * mm});
            skLineSegment(sketch, "E26.68", {"start": v(-0.28, -41.55) * mm, "end": v(35.28, -21.02) * mm});
            skLineSegment(sketch, "E26.69", {"start": v(35.28, -7.05) * mm, "end": v(23.19, -14.04) * mm});
            skLineSegment(sketch, "E26.70", {"start": v(53.06, 30.3) * mm, "end": v(35.28, 40.57) * mm});
            skLineSegment(sketch, "E26.71", {"start": v(-23.74, -28) * mm, "end": v(-23.74, -14.04) * mm});
            skLineSegment(sketch, "E26.72", {"start": v(-12.37, -48.54) * mm, "end": v(-0.28, -55.52) * mm});
            skLineSegment(sketch, "E26.73", {"start": v(-18.06, 30.3) * mm, "end": v(-0.28, 20.04) * mm});
            skLineSegment(sketch, "E26.74", {"start": v(53.06, 9.77) * mm, "end": v(53.06, 30.3) * mm});
            skLineSegment(sketch, "E26.75", {"start": v(-53.62, -10.76) * mm, "end": v(-53.62, -31.29) * mm});
            skLineSegment(sketch, "E26.76", {"start": v(35.28, -0.5) * mm, "end": v(17.5, -10.76) * mm});
            skCircle(sketch, "E26.77", {"center": v(-0.28, -0.5) * mm, "radius": 12.7 * mm});
            skArc(sketch, "E26.78", {"start": v(17.5, 30.3) * mm, "mid": v(53.06, 30.3) * mm, "end": v(35.28, -0.5) * mm});
            skLineSegment(sketch, "E26.79", {"start": v(-18.06, 9.77) * mm, "end": v(-0.28, -0.5) * mm});
            skLineSegment(sketch, "E26.80", {"start": v(-6.27, -3.95) * mm, "end": v(-24.05, 6.31) * mm});
            skLineSegment(sketch, "E26.81", {"start": v(17.5, -10.76) * mm, "end": v(17.5, -31.29) * mm});
            skLineSegment(sketch, "E26.82", {"start": v(-0.28, 26.6) * mm, "end": v(11.82, 33.58) * mm});
            skLineSegment(sketch, "E26.83", {"start": v(23.19, 13.05) * mm, "end": v(35.28, 6.07) * mm});
            skLineSegment(sketch, "E26.84", {"start": v(-23.74, -14.04) * mm, "end": v(-35.84, -7.05) * mm});
            skLineSegment(sketch, "E26.85", {"start": v(-0.28, -27.58) * mm, "end": v(-12.37, -34.57) * mm});
            skLineSegment(sketch, "E26.86", {"start": v(-0.28, 20.04) * mm, "end": v(17.5, 30.3) * mm});
            skLineSegment(sketch, "E26.87", {"start": v(-18.06, 50.83) * mm, "end": v(-18.06, 30.3) * mm});
            skLineSegment(sketch, "E26.88", {"start": v(-18.06, -10.76) * mm, "end": v(-35.84, -0.5) * mm});
            skLineSegment(sketch, "E26.89", {"start": v(17.5, -31.29) * mm, "end": v(35.28, -41.55) * mm});
            skArc(sketch, "E26.90", {"start": v(-33.27, 12.77) * mm, "mid": v(-31.07, 17.29) * mm, "end": v(-28.26, 21.45) * mm});
            skArc(sketch, "E26.91", {"start": v(-35.84, -0.5) * mm, "mid": v(-53.62, 30.3) * mm, "end": v(-18.06, 30.3) * mm});
            skLineSegment(sketch, "E26.92", {"start": v(-0.28, -21.02) * mm, "end": v(-0.28, -0.5) * mm});
            skLineSegment(sketch, "E26.93", {"start": v(-0.28, -0.5) * mm, "end": v(6.6, -4.46) * mm});
            skLineSegment(sketch, "E26.94", {"start": v(35.28, 6.07) * mm, "end": v(47.38, 13.05) * mm});
            skLineSegment(sketch, "E26.95", {"start": v(-12.37, 47.55) * mm, "end": v(-12.37, 33.58) * mm});
            skLineSegment(sketch, "E26.96", {"start": v(35.28, -41.55) * mm, "end": v(53.06, -31.29) * mm});
            skLineSegment(sketch, "E26.97", {"start": v(11.82, -48.54) * mm, "end": v(11.82, -34.57) * mm});
            skLineSegment(sketch, "E26.98", {"start": v(17.5, 50.83) * mm, "end": v(-0.28, 61.1) * mm});
            skLineSegment(sketch, "E26.99", {"start": v(17.5, -51.82) * mm, "end": v(17.5, -31.29) * mm});
            skLineSegment(sketch, "E26.100", {"start": v(53.06, -31.29) * mm, "end": v(53.06, -10.76) * mm});
            skArc(sketch, "E26.101", {"start": v(17.5, -31.29) * mm, "mid": v(-0.28, -62.08) * mm, "end": v(-18.06, -31.29) * mm});
            skLineSegment(sketch, "E26.102", {"start": v(-0.28, -0.5) * mm, "end": v(-0.28, 6.88) * mm});
            skLineSegment(sketch, "E26.103", {"start": v(53.06, -10.76) * mm, "end": v(35.28, -0.5) * mm});
            skLineSegment(sketch, "E26.104", {"start": v(47.38, 27.02) * mm, "end": v(35.28, 34) * mm});
            skLineSegment(sketch, "E26.105", {"start": v(17.5, -31.29) * mm, "end": v(-0.28, -21.02) * mm});
            skCircle(sketch, "E26.106", {"center": v(-35.84, -21.02) * mm, "radius": 13.97 * mm});
            skLineSegment(sketch, "E26.107", {"start": v(47.38, -14.04) * mm, "end": v(35.28, -7.05) * mm});
            skLineSegment(sketch, "E26.108", {"start": v(17.5, -31.29) * mm, "end": v(35.28, -41.55) * mm});
            skLineSegment(sketch, "E26.109", {"start": v(23.19, -28) * mm, "end": v(35.28, -35) * mm});
            skLineSegment(sketch, "E26.110", {"start": v(-18.06, -10.76) * mm, "end": v(-33.27, -1.97) * mm});
            skLineSegment(sketch, "E26.111", {"start": v(35.28, -0.5) * mm, "end": v(53.06, 9.77) * mm});
            skLineSegment(sketch, "E26.112", {"start": v(-0.28, 6.88) * mm, "end": v(-0.28, -0.5) * mm});
            skArc(sketch, "E27.trimOffspring", {"start": v(-21.83, 5.03) * mm, "mid": v(-27.13, 1.45) * mm, "end": v(-33.27, -0.33) * mm});
            skArc(sketch, "E28.trimOffspring", {"start": v(-23.74, 26.23) * mm, "mid": v(-18.06, 30.3) * mm, "end": v(-11.69, 33.19) * mm});
            skArc(sketch, "E29.trimOffspring", {"start": v(-16.91, 28) * mm, "mid": v(-15.34, 18.75) * mm, "end": v(-18.06, 9.77) * mm});
            skArc(sketch, "E30.trimOffspring", {"start": v(-5.3, 34.71) * mm, "mid": v(-0.28, 35.07) * mm, "end": v(4.74, 34.71) * mm});
            skArc(sketch, "E31.trimOffspring", {"start": v(5.66, 37.14) * mm, "mid": v(15.96, 33.98) * mm, "end": v(24.96, 28.05) * mm});
            skArc(sketch, "E32.trimOffspring", {"start": v(11.14, 33.19) * mm, "mid": v(17.5, 30.3) * mm, "end": v(23.19, 26.23) * mm});
            skArc(sketch, "E33.trimOffspring", {"start": v(8.68, 32.44) * mm, "mid": v(-0.28, 28.47) * mm, "end": v(-9.23, 32.44) * mm});
            skArc(sketch, "E34.trimOffspring", {"start": v(27.7, 21.45) * mm, "mid": v(30.52, 17.29) * mm, "end": v(32.72, 12.77) * mm});
            skArc(sketch, "E35.trimOffspring", {"start": v(35.28, 13.19) * mm, "mid": v(37.7, 2.68) * mm, "end": v(37.06, -8.08) * mm});
            skArc(sketch, "E36.trimOffspring", {"start": v(34.6, 6.47) * mm, "mid": v(35.28, -0.5) * mm, "end": v(34.6, -7.45) * mm});
            skArc(sketch, "E37.trimOffspring", {"start": v(16.08, 28.16) * mm, "mid": v(-0.28, 20.04) * mm, "end": v(-16.63, 28.16) * mm});
            skArc(sketch, "E38.trimOffspring", {"start": v(32.72, -0.33) * mm, "mid": v(23.93, 2.94) * mm, "end": v(17.5, 9.77) * mm});
            skArc(sketch, "E39.trimOffspring", {"start": v(32.72, -13.75) * mm, "mid": v(30.52, -18.27) * mm, "end": v(27.7, -22.44) * mm});
            skArc(sketch, "E40.trimOffspring", {"start": v(29.35, -24.45) * mm, "mid": v(21.46, -31.79) * mm, "end": v(11.82, -36.62) * mm});
            skArc(sketch, "E41.trimOffspring", {"start": v(23.19, -27.21) * mm, "mid": v(17.5, -31.29) * mm, "end": v(11.14, -34.17) * mm});
            skArc(sketch, "E42.trimOffspring", {"start": v(16.36, -28.99) * mm, "mid": v(17.5, -10.76) * mm, "end": v(32.72, -0.65) * mm});
            skArc(sketch, "E43.trimOffspring", {"start": v(-6.2, -38.13) * mm, "mid": v(-16.51, -34.96) * mm, "end": v(-25.51, -29.03) * mm});
            skArc(sketch, "E44.trimOffspring", {"start": v(-11.69, -34.17) * mm, "mid": v(-11.87, -34.1) * mm, "end": v(-12.06, -34.04) * mm});
            skArc(sketch, "E45.trimOffspring", {"start": v(4.74, -35.7) * mm, "mid": v(-0.28, -36.05) * mm, "end": v(-5.3, -35.7) * mm});
            skArc(sketch, "E46.trimOffspring", {"start": v(-18.06, -31.29) * mm, "mid": v(-21, -29.4) * mm, "end": v(-23.74, -27.21) * mm});
            skArc(sketch, "E47.trimOffspring", {"start": v(-18.06, -31.29) * mm, "mid": v(-53.62, -31.29) * mm, "end": v(-35.84, -0.5) * mm});
            skArc(sketch, "E48.trimOffspring", {"start": v(-28.26, -22.44) * mm, "mid": v(-31.07, -18.27) * mm, "end": v(-33.27, -13.75) * mm});
            skArc(sketch, "E49.trimOffspring", {"start": v(-35.84, -14.17) * mm, "mid": v(-38.38, -0.5) * mm, "end": v(-35.84, 13.19) * mm});
            skArc(sketch, "E50.trimOffspring", {"start": v(-35.15, -7.45) * mm, "mid": v(-35.84, -0.5) * mm, "end": v(-35.15, 6.47) * mm});
            skArc(sketch, "E51.trimOffspring", {"start": v(15.2, 15.8) * mm, "mid": v(14.85, 22) * mm, "end": v(16.36, 28) * mm});
            skArc(sketch, "E52.trimOffspring", {"start": v(6.6, -22.2) * mm, "mid": v(11.85, -24.98) * mm, "end": v(16.08, -29.15) * mm});
            skSolve(sketch);
        }
        {
            var Q0;
            Q0=makeQuery(id+"F1.opExtrude","CAP_FACE",FACE,{"disambiguationData":[OSD([sQuery(id+"F0.wireOp",EDGE,"E0"),sQuery(id+"F0.wireOp",EDGE,"E1.0"),sQuery(id+"F0.wireOp",EDGE,"E1.1"),sQuery(id+"F0.wireOp",EDGE,"E1.2"),sQuery(id+"F0.wireOp",EDGE,"E1.3"),sQuery(id+"F0.wireOp",EDGE,"E1.4"),sQuery(id+"F0.wireOp",EDGE,"E1.5"),sQuery(id+"F0.wireOp",EDGE,"E2.0"),sQuery(id+"F0.wireOp",EDGE,"E2.1"),sQuery(id+"F0.wireOp",EDGE,"E2.2"),sQuery(id+"F0.wireOp",EDGE,"E2.3"),sQuery(id+"F0.wireOp",EDGE,"E2.4"),sQuery(id+"F0.wireOp",EDGE,"E2.5"),sQuery(id+"F0.wireOp",EDGE,"E3.0"),sQuery(id+"F0.wireOp",EDGE,"E3.1"),sQuery(id+"F0.wireOp",EDGE,"E3.2"),sQuery(id+"F0.wireOp",EDGE,"E3.3"),sQuery(id+"F0.wireOp",EDGE,"E3.4"),sQuery(id+"F0.wireOp",EDGE,"E3.5"),sQuery(id+"F0.wireOp",EDGE,"E4.0"),sQuery(id+"F0.wireOp",EDGE,"E4.1"),sQuery(id+"F0.wireOp",EDGE,"E4.2"),sQuery(id+"F0.wireOp",EDGE,"E4.3"),sQuery(id+"F0.wireOp",EDGE,"E4.4"),sQuery(id+"F0.wireOp",EDGE,"E4.5"),sQuery(id+"F0.wireOp",EDGE,"E5.0"),sQuery(id+"F0.wireOp",EDGE,"E5.1"),sQuery(id+"F0.wireOp",EDGE,"E5.2"),sQuery(id+"F0.wireOp",EDGE,"E5.3"),sQuery(id+"F0.wireOp",EDGE,"E5.4"),sQuery(id+"F0.wireOp",EDGE,"E5.5"),sQuery(id+"F0.wireOp",EDGE,"E6.0"),sQuery(id+"F0.wireOp",EDGE,"E6.1"),sQuery(id+"F0.wireOp",EDGE,"E6.2"),sQuery(id+"F0.wireOp",EDGE,"E6.3"),sQuery(id+"F0.wireOp",EDGE,"E6.4"),sQuery(id+"F0.wireOp",EDGE,"E6.5"),sQuery(id+"F0.wireOp",EDGE,"E7.0"),sQuery(id+"F0.wireOp",EDGE,"E7.1"),sQuery(id+"F0.wireOp",EDGE,"E7.2"),sQuery(id+"F0.wireOp",EDGE,"E7.3"),sQuery(id+"F0.wireOp",EDGE,"E7.4"),sQuery(id+"F0.wireOp",EDGE,"E7.5"),sQuery(id+"F0.wireOp",EDGE,"E8.0"),sQuery(id+"F0.wireOp",EDGE,"E8.1"),sQuery(id+"F0.wireOp",EDGE,"E8.2"),sQuery(id+"F0.wireOp",EDGE,"E8.3"),sQuery(id+"F0.wireOp",EDGE,"E8.4"),sQuery(id+"F0.wireOp",EDGE,"E8.5"),sQuery(id+"F0.wireOp",EDGE,"E9.0"),sQuery(id+"F0.wireOp",EDGE,"E9.1"),sQuery(id+"F0.wireOp",EDGE,"E9.2"),sQuery(id+"F0.wireOp",EDGE,"E9.3"),sQuery(id+"F0.wireOp",EDGE,"E9.4"),sQuery(id+"F0.wireOp",EDGE,"E9.5"),sQuery(id+"F0.wireOp",EDGE,"E10.0"),sQuery(id+"F0.wireOp",EDGE,"E10.1"),sQuery(id+"F0.wireOp",EDGE,"E10.2"),sQuery(id+"F0.wireOp",EDGE,"E10.3"),sQuery(id+"F0.wireOp",EDGE,"E10.4"),sQuery(id+"F0.wireOp",EDGE,"E10.5"),sQuery(id+"F0.wireOp",EDGE,"E11.0"),sQuery(id+"F0.wireOp",EDGE,"E11.1"),sQuery(id+"F0.wireOp",EDGE,"E11.2"),sQuery(id+"F0.wireOp",EDGE,"E11.3"),sQuery(id+"F0.wireOp",EDGE,"E11.4"),sQuery(id+"F0.wireOp",EDGE,"E11.5"),sQuery(id+"F0.wireOp",EDGE,"E12.0"),sQuery(id+"F0.wireOp",EDGE,"E12.1"),sQuery(id+"F0.wireOp",EDGE,"E12.2"),sQuery(id+"F0.wireOp",EDGE,"E12.3"),sQuery(id+"F0.wireOp",EDGE,"E12.4"),sQuery(id+"F0.wireOp",EDGE,"E12.5"),sQuery(id+"F0.wireOp",EDGE,"E13.0"),sQuery(id+"F0.wireOp",EDGE,"E13.1"),sQuery(id+"F0.wireOp",EDGE,"E13.2"),sQuery(id+"F0.wireOp",EDGE,"E13.3"),sQuery(id+"F0.wireOp",EDGE,"E13.4"),sQuery(id+"F0.wireOp",EDGE,"E13.5"),sQuery(id+"F0.wireOp",EDGE,"E14"),sQuery(id+"F0.wireOp",EDGE,"E15"),sQuery(id+"F0.wireOp",EDGE,"E16"),sQuery(id+"F0.wireOp",EDGE,"E21"),sQuery(id+"F0.wireOp",EDGE,"E22"),sQuery(id+"F0.wireOp",EDGE,"E23"),sQuery(id+"F0.wireOp",EDGE,"E24"),sQuery(id+"F0.wireOp",EDGE,"E25.0"),sQuery(id+"F0.wireOp",EDGE,"E25.1"),sQuery(id+"F0.wireOp",EDGE,"E25.2"),sQuery(id+"F0.wireOp",EDGE,"E25.3"),sQuery(id+"F0.wireOp",EDGE,"E25.4"),sQuery(id+"F0.wireOp",EDGE,"E25.5")])],"isStart":false});
            var sketch = newSketch(context, id + "F3", { "sketchPlane" : qUnion([Q0])});
            skCircle(sketch, "E53.0", {"center": v(-0.28, 0.5) * mm, "radius": 15.24 * mm});
            skLineSegment(sketch, "E54.0", {"start": v(-6.27, 3.95) * mm, "end": v(-24.05, -6.31) * mm});
            skLineSegment(sketch, "E55.0", {"start": v(-18.06, -9.77) * mm, "end": v(-0.28, 0.5) * mm});
            skLineSegment(sketch, "E56.0", {"start": v(-35.84, 0.5) * mm, "end": v(-18.06, -9.77) * mm});
            skLineSegment(sketch, "E57.0", {"start": v(-33.27, -18.56) * mm, "end": v(-33.27, 19.54) * mm});
            skLineSegment(sketch, "E58.0", {"start": v(-35.84, -20.04) * mm, "end": v(-35.84, 21.02) * mm});
            skLineSegment(sketch, "E59.0", {"start": v(-0.28, -37.6) * mm, "end": v(-33.27, -18.56) * mm});
            skLineSegment(sketch, "E60.0", {"start": v(-0.28, -40.57) * mm, "end": v(-35.84, -20.04) * mm});
            skLineSegment(sketch, "E61.0", {"start": v(-18.06, -9.77) * mm, "end": v(-18.06, -30.3) * mm});
            skLineSegment(sketch, "E62.0", {"start": v(-0.28, -6.88) * mm, "end": v(17.5, -17.14) * mm});
            skLineSegment(sketch, "E63.0", {"start": v(-0.28, 0.5) * mm, "end": v(17.5, -9.77) * mm});
            skLineSegment(sketch, "E64.0", {"start": v(17.5, -30.3) * mm, "end": v(17.5, -9.77) * mm});
            skLineSegment(sketch, "E65.0", {"start": v(6.6, 4.46) * mm, "end": v(6.6, 24.99) * mm});
            skLineSegment(sketch, "E66.0", {"start": v(-0.28, 21.02) * mm, "end": v(-0.28, 0.5) * mm});
            skLineSegment(sketch, "E67.0", {"start": v(17.5, 31.29) * mm, "end": v(-0.28, 21.02) * mm});
            skLineSegment(sketch, "E68.0", {"start": v(-33.27, 19.54) * mm, "end": v(-0.28, 38.6) * mm});
            skLineSegment(sketch, "E69.0", {"start": v(-35.84, 21.02) * mm, "end": v(-0.28, 41.55) * mm});
            skLineSegment(sketch, "E70.0", {"start": v(-0.28, 21.02) * mm, "end": v(-18.06, 31.29) * mm});
            skLineSegment(sketch, "E71.0", {"start": v(-18.06, 31.29) * mm, "end": v(-18.06, 10.76) * mm});
            skLineSegment(sketch, "E72.0", {"start": v(32.72, 19.54) * mm, "end": v(32.72, -18.56) * mm});
            skLineSegment(sketch, "E73.0", {"start": v(35.28, 21.02) * mm, "end": v(35.28, -20.04) * mm});
            skLineSegment(sketch, "E74.0", {"start": v(32.72, -18.56) * mm, "end": v(-0.28, -37.6) * mm});
            skLineSegment(sketch, "E75.0", {"start": v(35.28, -20.04) * mm, "end": v(-0.28, -40.57) * mm});
            skLineSegment(sketch, "E76.0", {"start": v(-0.28, -20.04) * mm, "end": v(17.5, -30.3) * mm});
            skLineSegment(sketch, "E77.0", {"start": v(-18.06, -30.3) * mm, "end": v(-0.28, -20.04) * mm});
            skLineSegment(sketch, "E78.0", {"start": v(17.5, 10.76) * mm, "end": v(17.5, 31.29) * mm});
            skLineSegment(sketch, "E79.0", {"start": v(35.28, 0.5) * mm, "end": v(17.5, 10.76) * mm});
            skLineSegment(sketch, "E80.0", {"start": v(17.5, -9.77) * mm, "end": v(35.28, 0.5) * mm});
            skLineSegment(sketch, "E81.0", {"start": v(23.19, -13.05) * mm, "end": v(35.28, -6.07) * mm});
            skLineSegment(sketch, "E82.0", {"start": v(23.19, -27.02) * mm, "end": v(23.19, -13.05) * mm});
            skLineSegment(sketch, "E83.0", {"start": v(-0.28, -26.6) * mm, "end": v(11.82, -33.58) * mm});
            skLineSegment(sketch, "E84.0", {"start": v(-12.37, -33.58) * mm, "end": v(-0.28, -26.6) * mm});
            skLineSegment(sketch, "E85.0", {"start": v(-23.74, -13.05) * mm, "end": v(-23.74, -27.02) * mm});
            skLineSegment(sketch, "E86.0", {"start": v(-35.84, -6.07) * mm, "end": v(-23.74, -13.05) * mm});
            skLineSegment(sketch, "E87.0", {"start": v(35.28, 7.05) * mm, "end": v(23.19, 14.04) * mm});
            skLineSegment(sketch, "E88.0", {"start": v(23.19, 14.04) * mm, "end": v(23.19, 28) * mm});
            skLineSegment(sketch, "E89.0", {"start": v(-0.28, 27.58) * mm, "end": v(-12.37, 34.57) * mm});
            skLineSegment(sketch, "E90.0", {"start": v(11.82, 34.57) * mm, "end": v(-0.28, 27.58) * mm});
            skLineSegment(sketch, "E91.0", {"start": v(-23.74, 28) * mm, "end": v(-23.74, 14.04) * mm});
            skLineSegment(sketch, "E92.0", {"start": v(-23.74, 14.04) * mm, "end": v(-35.84, 7.05) * mm});
            skLineSegment(sketch, "E93.0", {"start": v(-18.06, 10.76) * mm, "end": v(-35.84, 0.5) * mm});
            skLineSegment(sketch, "E94.0", {"start": v(-0.28, 38.6) * mm, "end": v(32.72, 19.54) * mm});
            skLineSegment(sketch, "E95.0", {"start": v(-0.28, 41.55) * mm, "end": v(35.28, 21.02) * mm});
            skSolve(sketch);
        }
        {
            var Q0;
            {var subQ7=sQuery(id+"F3.wireOp",EDGE,"E68.0");var subQ8=sQuery(id+"F3.wireOp",EDGE,"E57.0");var subQ9=makeQuery(id+"F3.imprint","INTERSECT",VERTEX,{"derivedFrom":[subQ8,subQ7]});Q0=makeQuery(id+"F3.imprint","IMPRINT",FACE,{"disambiguationData":[TD([[makeQuery(id+"F3.imprint","IMPRINT",EDGE,{"disambiguationData":[TD([[subQ9,1.0]])],"derivedFrom":subQ8}),1.0]])]});}
            var Q1;
            {var subQ3=sQuery(id+"F3.wireOp",EDGE,"E68.0");var subQ9=sQuery(id+"F3.wireOp",EDGE,"E94.0");var subQ11=makeQuery(id+"F3.imprint","INTERSECT",VERTEX,{"derivedFrom":[subQ3,subQ9]});Q1=makeQuery(id+"F3.imprint","IMPRINT",FACE,{"disambiguationData":[TD([[makeQuery(id+"F3.imprint","IMPRINT",EDGE,{"disambiguationData":[TD([[subQ11,1.0]])],"derivedFrom":subQ3}),1.0]])]});}
            var Q2;
            {var subQ3=sQuery(id+"F3.wireOp",EDGE,"E94.0");var subQ8=sQuery(id+"F3.wireOp",EDGE,"E72.0");var subQ11=makeQuery(id+"F3.imprint","INTERSECT",VERTEX,{"derivedFrom":[subQ8,subQ3]});Q2=makeQuery(id+"F3.imprint","IMPRINT",FACE,{"disambiguationData":[TD([[makeQuery(id+"F3.imprint","IMPRINT",EDGE,{"disambiguationData":[TD([[subQ11,-1.0]])],"derivedFrom":subQ8}),1.0]])]});}
            var Q3;
            {var subQ7=sQuery(id+"F3.wireOp",EDGE,"E74.0");var subQ9=sQuery(id+"F3.wireOp",EDGE,"E72.0");var subQ10=makeQuery(id+"F3.imprint","INTERSECT",VERTEX,{"derivedFrom":[subQ9,subQ7]});Q3=makeQuery(id+"F3.imprint","IMPRINT",FACE,{"disambiguationData":[TD([[makeQuery(id+"F3.imprint","IMPRINT",EDGE,{"disambiguationData":[TD([[subQ10,1.0]])],"derivedFrom":subQ9}),1.0]])]});}
            var Q4;
            {var subQ5=sQuery(id+"F3.wireOp",EDGE,"E74.0");var subQ6=sQuery(id+"F3.wireOp",EDGE,"E59.0");var subQ7=makeQuery(id+"F3.imprint","INTERSECT",VERTEX,{"derivedFrom":[subQ6,subQ5]});Q4=makeQuery(id+"F3.imprint","IMPRINT",FACE,{"disambiguationData":[TD([[makeQuery(id+"F3.imprint","IMPRINT",EDGE,{"disambiguationData":[TD([[subQ7,-1.0]])],"derivedFrom":subQ6}),1.0]])]});}
            var Q5;
            {var subQ5=sQuery(id+"F3.wireOp",EDGE,"E59.0");var subQ6=sQuery(id+"F3.wireOp",EDGE,"E57.0");var subQ7=makeQuery(id+"F3.imprint","INTERSECT",VERTEX,{"derivedFrom":[subQ6,subQ5]});Q5=makeQuery(id+"F3.imprint","IMPRINT",FACE,{"disambiguationData":[TD([[makeQuery(id+"F3.imprint","IMPRINT",EDGE,{"disambiguationData":[TD([[subQ7,-1.0]])],"derivedFrom":subQ6}),1.0]])]});}
            var Q6;
            {var subQ0=sQuery(id+"F3.wireOp",EDGE,"E63.0");var subQ1=sQuery(id+"F3.wireOp",EDGE,"E53.0");var subQ2=makeQuery(id+"F3.imprint","INTERSECT",VERTEX,{"derivedFrom":[subQ1,subQ0]});Q6=makeQuery(id+"F3.imprint","IMPRINT",FACE,{"disambiguationData":[TD([[makeQuery(id+"F3.imprint","IMPRINT",EDGE,{"disambiguationData":[TD([[subQ2,1.0]])],"derivedFrom":subQ1}),-1.0]])]});}
            var Q7;
            {var subQ0=sQuery(id+"F3.wireOp",EDGE,"E55.0");var subQ1=sQuery(id+"F3.wireOp",EDGE,"E53.0");var subQ2=makeQuery(id+"F3.imprint","INTERSECT",VERTEX,{"derivedFrom":[subQ1,subQ0]});Q7=makeQuery(id+"F3.imprint","IMPRINT",FACE,{"disambiguationData":[TD([[makeQuery(id+"F3.imprint","IMPRINT",EDGE,{"disambiguationData":[TD([[subQ2,1.0]])],"derivedFrom":subQ1}),-1.0]])]});}
            var Q8;
            {var subQ0=sQuery(id+"F3.wireOp",EDGE,"E66.0");var subQ1=sQuery(id+"F3.wireOp",EDGE,"E53.0");var subQ2=makeQuery(id+"F3.imprint","INTERSECT",VERTEX,{"derivedFrom":[subQ1,subQ0]});Q8=makeQuery(id+"F3.imprint","IMPRINT",FACE,{"disambiguationData":[TD([[makeQuery(id+"F3.imprint","IMPRINT",EDGE,{"disambiguationData":[TD([[subQ2,1.0]])],"derivedFrom":subQ1}),-1.0]])]});}
            extrude(context, id + "F4", {"entities" : qUnion([Q0, Q1, Q2, Q3, Q4, Q5, Q6, Q7, Q8]), "operationType" : NewBodyOperationType.REMOVE, "oppositeDirection" : true, "depth" : 2.03 * mm, "offsetDistance" : 25.4 * mm});
        }
        {
            var Q0;
            Q0=makeQuery(id+"F1.opExtrude","CAP_FACE",FACE,{"disambiguationData":[OSD([sQuery(id+"F0.wireOp",EDGE,"E0"),sQuery(id+"F0.wireOp",EDGE,"E1.0"),sQuery(id+"F0.wireOp",EDGE,"E1.1"),sQuery(id+"F0.wireOp",EDGE,"E1.2"),sQuery(id+"F0.wireOp",EDGE,"E1.3"),sQuery(id+"F0.wireOp",EDGE,"E1.4"),sQuery(id+"F0.wireOp",EDGE,"E1.5"),sQuery(id+"F0.wireOp",EDGE,"E2.0"),sQuery(id+"F0.wireOp",EDGE,"E2.1"),sQuery(id+"F0.wireOp",EDGE,"E2.2"),sQuery(id+"F0.wireOp",EDGE,"E2.3"),sQuery(id+"F0.wireOp",EDGE,"E2.4"),sQuery(id+"F0.wireOp",EDGE,"E2.5"),sQuery(id+"F0.wireOp",EDGE,"E3.0"),sQuery(id+"F0.wireOp",EDGE,"E3.1"),sQuery(id+"F0.wireOp",EDGE,"E3.2"),sQuery(id+"F0.wireOp",EDGE,"E3.3"),sQuery(id+"F0.wireOp",EDGE,"E3.4"),sQuery(id+"F0.wireOp",EDGE,"E3.5"),sQuery(id+"F0.wireOp",EDGE,"E4.0"),sQuery(id+"F0.wireOp",EDGE,"E4.1"),sQuery(id+"F0.wireOp",EDGE,"E4.2"),sQuery(id+"F0.wireOp",EDGE,"E4.3"),sQuery(id+"F0.wireOp",EDGE,"E4.4"),sQuery(id+"F0.wireOp",EDGE,"E4.5"),sQuery(id+"F0.wireOp",EDGE,"E5.0"),sQuery(id+"F0.wireOp",EDGE,"E5.1"),sQuery(id+"F0.wireOp",EDGE,"E5.2"),sQuery(id+"F0.wireOp",EDGE,"E5.3"),sQuery(id+"F0.wireOp",EDGE,"E5.4"),sQuery(id+"F0.wireOp",EDGE,"E5.5"),sQuery(id+"F0.wireOp",EDGE,"E6.0"),sQuery(id+"F0.wireOp",EDGE,"E6.1"),sQuery(id+"F0.wireOp",EDGE,"E6.2"),sQuery(id+"F0.wireOp",EDGE,"E6.3"),sQuery(id+"F0.wireOp",EDGE,"E6.4"),sQuery(id+"F0.wireOp",EDGE,"E6.5"),sQuery(id+"F0.wireOp",EDGE,"E7.0"),sQuery(id+"F0.wireOp",EDGE,"E7.1"),sQuery(id+"F0.wireOp",EDGE,"E7.2"),sQuery(id+"F0.wireOp",EDGE,"E7.3"),sQuery(id+"F0.wireOp",EDGE,"E7.4"),sQuery(id+"F0.wireOp",EDGE,"E7.5"),sQuery(id+"F0.wireOp",EDGE,"E8.0"),sQuery(id+"F0.wireOp",EDGE,"E8.1"),sQuery(id+"F0.wireOp",EDGE,"E8.2"),sQuery(id+"F0.wireOp",EDGE,"E8.3"),sQuery(id+"F0.wireOp",EDGE,"E8.4"),sQuery(id+"F0.wireOp",EDGE,"E8.5"),sQuery(id+"F0.wireOp",EDGE,"E9.0"),sQuery(id+"F0.wireOp",EDGE,"E9.1"),sQuery(id+"F0.wireOp",EDGE,"E9.2"),sQuery(id+"F0.wireOp",EDGE,"E9.3"),sQuery(id+"F0.wireOp",EDGE,"E9.4"),sQuery(id+"F0.wireOp",EDGE,"E9.5"),sQuery(id+"F0.wireOp",EDGE,"E10.0"),sQuery(id+"F0.wireOp",EDGE,"E10.1"),sQuery(id+"F0.wireOp",EDGE,"E10.2"),sQuery(id+"F0.wireOp",EDGE,"E10.3"),sQuery(id+"F0.wireOp",EDGE,"E10.4"),sQuery(id+"F0.wireOp",EDGE,"E10.5"),sQuery(id+"F0.wireOp",EDGE,"E11.0"),sQuery(id+"F0.wireOp",EDGE,"E11.1"),sQuery(id+"F0.wireOp",EDGE,"E11.2"),sQuery(id+"F0.wireOp",EDGE,"E11.3"),sQuery(id+"F0.wireOp",EDGE,"E11.4"),sQuery(id+"F0.wireOp",EDGE,"E11.5"),sQuery(id+"F0.wireOp",EDGE,"E12.0"),sQuery(id+"F0.wireOp",EDGE,"E12.1"),sQuery(id+"F0.wireOp",EDGE,"E12.2"),sQuery(id+"F0.wireOp",EDGE,"E12.3"),sQuery(id+"F0.wireOp",EDGE,"E12.4"),sQuery(id+"F0.wireOp",EDGE,"E12.5"),sQuery(id+"F0.wireOp",EDGE,"E13.0"),sQuery(id+"F0.wireOp",EDGE,"E13.1"),sQuery(id+"F0.wireOp",EDGE,"E13.2"),sQuery(id+"F0.wireOp",EDGE,"E13.3"),sQuery(id+"F0.wireOp",EDGE,"E13.4"),sQuery(id+"F0.wireOp",EDGE,"E13.5"),sQuery(id+"F0.wireOp",EDGE,"E14"),sQuery(id+"F0.wireOp",EDGE,"E15"),sQuery(id+"F0.wireOp",EDGE,"E16"),sQuery(id+"F0.wireOp",EDGE,"E21"),sQuery(id+"F0.wireOp",EDGE,"E22"),sQuery(id+"F0.wireOp",EDGE,"E23"),sQuery(id+"F0.wireOp",EDGE,"E24"),sQuery(id+"F0.wireOp",EDGE,"E25.0"),sQuery(id+"F0.wireOp",EDGE,"E25.1"),sQuery(id+"F0.wireOp",EDGE,"E25.2"),sQuery(id+"F0.wireOp",EDGE,"E25.3"),sQuery(id+"F0.wireOp",EDGE,"E25.4"),sQuery(id+"F0.wireOp",EDGE,"E25.5")])],"isStart":true});
            var sketch = newSketch(context, id + "F5", { "sketchPlane" : qUnion([Q0])});
            skSolve(sketch);
        }
        {
            var Q0;
            {var subQ8=sQuery(id+"F2.wireOp",EDGE,"E26.8");var subQ11=sQuery(id+"F2.wireOp",EDGE,"E26.1");var subQ17=makeQuery(id+"F2.imprint","INTERSECT",VERTEX,{"derivedFrom":[subQ11,subQ8]});Q0=makeQuery(id+"F2.imprint","IMPRINT",FACE,{"disambiguationData":[TD([[makeQuery(id+"F2.imprint","IMPRINT",EDGE,{"disambiguationData":[TD([[subQ17,-1.0]])],"derivedFrom":subQ11}),-1.0]])]});}
            var Q1;
            {var subQ1=sQuery(id+"F2.wireOp",EDGE,"E26.24");var subQ4=sQuery(id+"F2.wireOp",EDGE,"E26.43");var subQ5=makeQuery(id+"F2.imprint","INTERSECT",VERTEX,{"derivedFrom":[subQ1,subQ4]});Q1=makeQuery(id+"F2.imprint","IMPRINT",FACE,{"disambiguationData":[TD([[makeQuery(id+"F2.imprint","IMPRINT",EDGE,{"disambiguationData":[TD([[subQ5,-1.0]])],"derivedFrom":subQ1}),-1.0]])]});}
            var Q2;
            {var subQ9=sQuery(id+"F2.wireOp",EDGE,"E26.24");var subQ11=sQuery(id+"F2.wireOp",EDGE,"E26.85");var subQ12=makeQuery(id+"F2.imprint","INTERSECT",VERTEX,{"derivedFrom":[subQ9,subQ11]});Q2=makeQuery(id+"F2.imprint","IMPRINT",FACE,{"disambiguationData":[TD([[makeQuery(id+"F2.imprint","IMPRINT",EDGE,{"disambiguationData":[TD([[subQ12,-1.0]])],"derivedFrom":subQ9}),-1.0]])]});}
            var Q3;
            {var subQ0=sQuery(id+"F2.wireOp",EDGE,"E26.58");var subQ1=sQuery(id+"F2.wireOp",EDGE,"E26.7");var subQ2=makeQuery(id+"F2.imprint","INTERSECT",VERTEX,{"derivedFrom":[subQ1,subQ0]});Q3=makeQuery(id+"F2.imprint","IMPRINT",FACE,{"disambiguationData":[TD([[makeQuery(id+"F2.imprint","IMPRINT",EDGE,{"disambiguationData":[TD([[subQ2,-1.0]])],"derivedFrom":subQ1}),-1.0]])]});}
            var Q4;
            {var subQ0=sQuery(id+"F2.wireOp",EDGE,"E26.83");var subQ1=sQuery(id+"F2.wireOp",EDGE,"E26.7");var subQ2=makeQuery(id+"F2.imprint","INTERSECT",VERTEX,{"derivedFrom":[subQ1,subQ0]});Q4=makeQuery(id+"F2.imprint","IMPRINT",FACE,{"disambiguationData":[TD([[makeQuery(id+"F2.imprint","IMPRINT",EDGE,{"disambiguationData":[TD([[subQ2,-1.0]])],"derivedFrom":subQ1}),-1.0]])]});}
            var Q5;
            {var subQ8=sQuery(id+"F2.wireOp",EDGE,"E26.1");var subQ11=sQuery(id+"F2.wireOp",EDGE,"E26.50");var subQ12=makeQuery(id+"F2.imprint","INTERSECT",VERTEX,{"derivedFrom":[subQ8,subQ11]});Q5=makeQuery(id+"F2.imprint","IMPRINT",FACE,{"disambiguationData":[TD([[makeQuery(id+"F2.imprint","IMPRINT",EDGE,{"disambiguationData":[TD([[subQ12,-1.0]])],"derivedFrom":subQ8}),-1.0]])]});}
            var Q6;
            {var subQ1=sQuery(id+"F2.wireOp",EDGE,"E26.49");var subQ4=sQuery(id+"F2.wireOp",EDGE,"E26.79");var subQ7=makeQuery(id+"F2.imprint","INTERSECT",VERTEX,{"derivedFrom":[subQ1,subQ4]});Q6=makeQuery(id+"F2.imprint","IMPRINT",FACE,{"disambiguationData":[TD([[makeQuery(id+"F2.imprint","IMPRINT",EDGE,{"disambiguationData":[TD([[subQ7,1.0]])],"derivedFrom":subQ1}),1.0]])]});}
            var Q7;
            {var subQ3=sQuery(id+"F2.wireOp",EDGE,"E26.49");var subQ5=sQuery(id+"F2.wireOp",EDGE,"E26.13");var subQ8=makeQuery(id+"F2.imprint","INTERSECT",VERTEX,{"derivedFrom":[subQ5,subQ3]});Q7=makeQuery(id+"F2.imprint","IMPRINT",FACE,{"disambiguationData":[TD([[makeQuery(id+"F2.imprint","IMPRINT",EDGE,{"disambiguationData":[TD([[subQ8,-1.0]])],"derivedFrom":subQ5}),-1.0]])]});}
            var Q8;
            {var subQ1=sQuery(id+"F2.wireOp",EDGE,"E26.92");var subQ3=sQuery(id+"F2.wireOp",EDGE,"E26.49");var subQ4=makeQuery(id+"F2.imprint","INTERSECT",VERTEX,{"derivedFrom":[subQ3,subQ1]});Q8=makeQuery(id+"F2.imprint","IMPRINT",FACE,{"disambiguationData":[TD([[makeQuery(id+"F2.imprint","IMPRINT",EDGE,{"disambiguationData":[TD([[subQ4,1.0]])],"derivedFrom":subQ3}),1.0]])]});}
            extrude(context, id + "F6", {"entities" : qUnion([Q0, Q1, Q2, Q3, Q4, Q5, Q6, Q7, Q8]), "operationType" : NewBodyOperationType.REMOVE, "oppositeDirection" : true, "depth" : 2.03 * mm, "offsetDistance" : 25.4 * mm});
        }
    });
